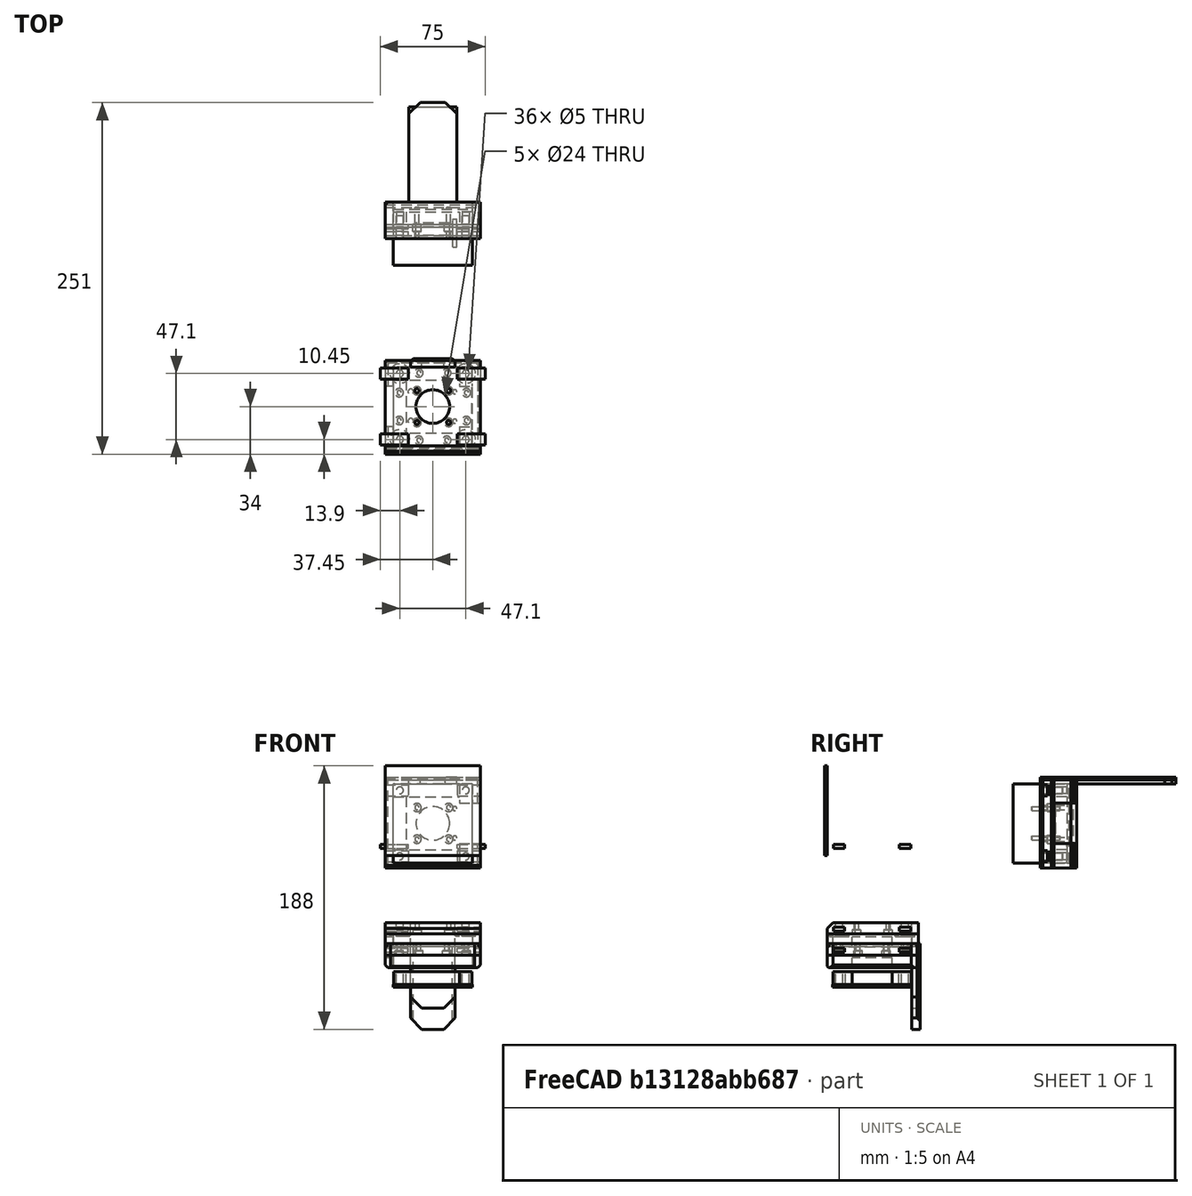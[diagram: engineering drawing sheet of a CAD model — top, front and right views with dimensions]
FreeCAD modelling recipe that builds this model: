
FCSTD DOCUMENT  (FreeCAD 0.19R24276 (Git))
Label: bazovina-part-K-moto-hold_028
License: All rights reserved
LicenseURL: http://en.wikipedia.org/wiki/All_rights_reserved
objects: Part::Cylinder×184, Part::Box×106, Part::Compound×93, Part::Cut×78, Part::Chamfer×16, Part::Common×6, Mesh::Feature×3
note: 483 computed .brp shape members not serialized (recipe doc carries the construction recipe); baked Part::Feature solids carry a one-line shape summary decoded from their .brp

FEATURE [Part::Box] Box131  label="Krychle131"
  AttacherType = Attacher::AttachEngine3D
  Height = 9
  Length = 14.62
  Placement = pos=(-58,38,63) rot=(0,0,1;0rad)
  Width = 10
FEATURE [Part::Cylinder] Cylinder280  label="Válec280"
  Angle = 360
  AttacherType = Attacher::AttachEngine3D
  Height = 50
  Placement = pos=(-23.55,-23.55,20) rot=(0,0,1;0rad)
  Radius = 2.5
FEATURE [Part::Box] Box130  label="Krychle130"
  AttacherType = Attacher::AttachEngine3D
  Height = 9
  Length = 10
  Placement = pos=(-58,-10,63) rot=(0,0,1;0rad)
  Width = 48
FEATURE [Part::Box] Box132  label="Krychle132"
  AttacherType = Attacher::AttachEngine3D
  Height = 9
  Length = 38
  Placement = pos=(-48,-10,63) rot=(0,0,1;0rad)
  Width = 10
FEATURE [Part::Cylinder] Cylinder281  label="Válec281"
  Angle = 360
  AttacherType = Attacher::AttachEngine3D
  Height = 50
  Placement = pos=(23.55,23.55,20) rot=(0,0,1;0rad)
  Radius = 2.5
FEATURE [Part::Box] Box133  label="Krychle133"
  AttacherType = Attacher::AttachEngine3D
  Height = 9
  Length = 14.62
  Placement = pos=(-14.615,38,63) rot=(0,0,1;0rad)
  Width = 10
FEATURE [Part::Cylinder] Cylinder282  label="Válec282"
  Angle = 360
  AttacherType = Attacher::AttachEngine3D
  Height = 50
  Placement = pos=(-23.55,23.55,20) rot=(0,0,1;0rad)
  Radius = 2.5
FEATURE [Part::Box] Box134  label="Krychle134"
  AttacherType = Attacher::AttachEngine3D
  Height = 9
  Length = 10
  Placement = pos=(-10,-10,63) rot=(0,0,1;0rad)
  Width = 48
FEATURE [Part::Compound] Compound277
  Links = -> [Box131,Box134,Box130,Box133,Box132]
  Placement = pos=(29,-19,-4) rot=(0,0,1;0rad)
FEATURE [Part::Cylinder] Cylinder283  label="Válec283"
  Angle = 360
  AttacherType = Attacher::AttachEngine3D
  Height = 50
  Placement = pos=(23.55,-23.55,20) rot=(0,0,1;0rad)
  Radius = 2.5
FEATURE [Part::Compound] Compound276
  Links = -> [Cylinder281,Cylinder283,Cylinder280,Cylinder282]
FEATURE [Part::Cut] Cut125
  Base = -> Compound277
  Placement = pos=(0,198,49) rot=(0.57735,0.57735,-0.57735;2.0944rad)
  Tool = -> Compound276
FEATURE [Part::Box] Box142  label="Krychle142"
  AttacherType = Attacher::AttachEngine3D
  Height = 18
  Length = 64
  Placement = pos=(-32,-34,32) rot=(0,0,1;0rad)
  Width = 68
FEATURE [Part::Cylinder] Cylinder588  label="Válec588"
  Angle = 360
  AttacherType = Attacher::AttachEngine3D
  Height = 20
  Placement = pos=(-7,-34,37) rot=(1,0,0;1.5708rad)
  Radius = 1.5
FEATURE [Part::Cylinder] Cylinder303  label="Válec303"
  Angle = 360
  AttacherType = Attacher::AttachEngine3D
  Height = 20
  Placement = pos=(7,-34,37) rot=(1,0,0;1.5708rad)
  Radius = 1.5
FEATURE [Part::Box] Box143  label="Krychle143"
  AttacherType = Attacher::AttachEngine3D
  Height = 6
  Length = 10
  Placement = pos=(3,-48,70) rot=(0,0,1;0rad)
  Width = 2
FEATURE [Part::Cylinder] Cylinder593  label="Válec593"
  Angle = 360
  AttacherType = Attacher::AttachEngine3D
  Height = 5
  Placement = pos=(2e-15,16,2) rot=(0,0,-1;1.1781rad)
  Radius = 3
FEATURE [Part::Box] Box225  label="Krychle225"
  AttacherType = Attacher::AttachEngine3D
  Height = 8
  Length = 68
  Placement = pos=(-34,-32,24) rot=(0,0,1;0rad)
  Width = 64
FEATURE [Part::Cylinder] Cylinder317  label="Válec317"
  Angle = 360
  AttacherType = Attacher::AttachEngine3D
  Height = 30
  Placement = pos=(-1.2e-14,-16,2) rot=(0,0,1;1.96349rad)
  Radius = 1.5
FEATURE [Part::Box] Box140  label="Krychle140"
  AttacherType = Attacher::AttachEngine3D
  Height = 6
  Length = 10
  Placement = pos=(-11,-48,70) rot=(0,0,1;0rad)
  Width = 2
FEATURE [Part::Box] Box139  label="Krychle139"
  AttacherType = Attacher::AttachEngine3D
  Height = 6
  Length = 10
  Placement = pos=(3,-48,34) rot=(0,0,1;0rad)
  Width = 2
FEATURE [Part::Box] Box223  label="Krychle223"
  AttacherType = Attacher::AttachEngine3D
  Height = 40
  Length = 56.5
  Placement = pos=(-28.25,-28.25,32) rot=(0,0,1;0rad)
  Width = 56.5
FEATURE [Part::Cut] Cut231
  Base = -> Box142
  Tool = -> Box223
FEATURE [Part::Compound] Compound283  label="hrubo_holder010"
  Links = -> [Cut231]
FEATURE [Part::Compound] Compound366  label="hrubo_holder011"
  Links = -> [Compound283]
FEATURE [Part::Box] Box141  label="Krychle141"
  AttacherType = Attacher::AttachEngine3D
  Height = 20
  Length = 28.8
  Placement = pos=(-14.4,-8,34) rot=(0,0,1;0rad)
  Width = 43.38
FEATURE [Part::Cut] Cut230
  Base = -> Compound366
  Placement = pos=(-29,18,30) rot=(0,0,1;0rad)
  Tool = -> Box141
FEATURE [Part::Compound] Compound361
  Links = -> [Cut230]
  Placement = pos=(-18,-29,-30) rot=(0,0,-1;1.5708rad)
FEATURE [Part::Compound] Compound287  label="hrubo_holder_nuovo003"
  Links = -> [Compound361]
FEATURE [Part::Compound] Compound365  label="hrubo_holder012"
  Links = -> [Compound287]
FEATURE [Part::Cylinder] Cylinder305  label="Válec305"
  Angle = 360
  AttacherType = Attacher::AttachEngine3D
  Height = 20
  Placement = pos=(-7,-34,73) rot=(1,0,0;1.5708rad)
  Radius = 1.5
FEATURE [Part::Cylinder] Cylinder306  label="Válec306"
  Angle = 360
  AttacherType = Attacher::AttachEngine3D
  Height = 20
  Placement = pos=(7,-34,73) rot=(1,0,0;1.5708rad)
  Radius = 1.5
FEATURE [Part::Compound] Compound279
  Links = -> [Cylinder303,Cylinder588,Cylinder306,Cylinder305]
FEATURE [Part::Cut] Cut228
  Base = -> Compound365
  Tool = -> Compound279
FEATURE [Part::Cylinder] Cylinder592  label="Válec592"
  Angle = 360
  AttacherType = Attacher::AttachEngine3D
  Height = 4
  Placement = pos=(-23.55,-23.55,26) rot=(0,0,1;0rad)
  Radius = 5
FEATURE [Part::Cylinder] Cylinder600  label="Válec600"
  Angle = 360
  AttacherType = Attacher::AttachEngine3D
  Height = 5
  Placement = pos=(16,0,2) rot=(0,0,1;3.53429rad)
  Radius = 3
FEATURE [Part::Cylinder] Cylinder595  label="Válec595"
  Angle = 360
  AttacherType = Attacher::AttachEngine3D
  Height = 5
  Placement = pos=(-16,7e-15,2) rot=(0,0,1;0.392699rad)
  Radius = 3
FEATURE [Part::Cylinder] Cylinder603  label="Válec603"
  Angle = 360
  AttacherType = Attacher::AttachEngine3D
  Height = 30
  Placement = pos=(2e-15,16,2) rot=(0,0,-1;1.1781rad)
  Radius = 1.5
FEATURE [Part::Cylinder] Cylinder605  label="Válec605"
  Angle = 360
  AttacherType = Attacher::AttachEngine3D
  Height = 4
  Placement = pos=(-23.55,23.55,26) rot=(0,0,1;0rad)
  Radius = 5
FEATURE [Part::Cylinder] Cylinder597  label="Válec597"
  Angle = 360
  AttacherType = Attacher::AttachEngine3D
  Height = 4
  Placement = pos=(23.55,-23.55,26) rot=(0,0,1;0rad)
  Radius = 5
FEATURE [Part::Cylinder] Cylinder601  label="Válec601"
  Angle = 360
  AttacherType = Attacher::AttachEngine3D
  Height = 20
  Placement = pos=(-23.55,23.55,20) rot=(0,0,1;0rad)
  Radius = 2.5
FEATURE [Part::Cylinder] Cylinder594  label="Válec594"
  Angle = 360
  AttacherType = Attacher::AttachEngine3D
  Height = 4
  Placement = pos=(23.55,23.55,26) rot=(0,0,1;0rad)
  Radius = 5
FEATURE [Part::Compound] Compound370
  Links = -> [Cylinder592,Cylinder594,Cylinder597,Cylinder605]
  Placement = pos=(0,0,-50) rot=(0,0,1;0rad)
FEATURE [Part::Box] Box144  label="Krychle144"
  AttacherType = Attacher::AttachEngine3D
  Height = 6
  Length = 10
  Placement = pos=(-11,-48,34) rot=(0,0,1;0rad)
  Width = 2
FEATURE [Part::Compound] Compound362
  Links = -> [Box139,Box144,Box143,Box140]
  Placement = pos=(0,9.75,0) rot=(0,0,1;0rad)
FEATURE [Part::Cut] Cut229  label="motor_holder001"
  Base = -> Cut228
  Tool = -> Compound362
FEATURE [Part::Box] Box227  label="Krychle227"
  AttacherType = Attacher::AttachEngine3D
  Height = 3
  Length = 20
  Placement = pos=(-37.45,19.55,26) rot=(0,0,1;0rad)
  Width = 8
FEATURE [Part::Box] Box228  label="Krychle228"
  AttacherType = Attacher::AttachEngine3D
  Height = 3
  Length = 20
  Placement = pos=(17.55,19.55,26) rot=(0,0,1;0rad)
  Width = 8
FEATURE [Part::Cylinder] Cylinder598  label="Válec598"
  Angle = 360
  AttacherType = Attacher::AttachEngine3D
  Height = 20
  Placement = pos=(-23.55,-23.55,20) rot=(0,0,1;0rad)
  Radius = 2.5
FEATURE [Part::Cylinder] Cylinder599  label="Válec599"
  Angle = 360
  AttacherType = Attacher::AttachEngine3D
  Height = 20
  Placement = pos=(0,0,15) rot=(0,0,1;0rad)
  Radius = 12
FEATURE [Part::Box] Box226  label="Krychle226"
  AttacherType = Attacher::AttachEngine3D
  Height = 3
  Length = 20
  Placement = pos=(17.55,-27.55,26) rot=(0,0,1;0rad)
  Width = 8
FEATURE [Part::Cylinder] Cylinder596  label="Válec596"
  Angle = 360
  AttacherType = Attacher::AttachEngine3D
  Height = 30
  Placement = pos=(-16,7e-15,2) rot=(0,0,1;0.392699rad)
  Radius = 1.5
FEATURE [Part::Box] Box229  label="Krychle229"
  AttacherType = Attacher::AttachEngine3D
  Height = 3
  Length = 20
  Placement = pos=(-37.45,-27.55,26) rot=(0,0,1;0rad)
  Width = 8
FEATURE [Part::Compound] Compound371
  Links = -> [Box228,Box226,Box227,Box229]
FEATURE [Part::Cylinder] Cylinder602  label="Válec602"
  Angle = 360
  AttacherType = Attacher::AttachEngine3D
  Height = 30
  Placement = pos=(16,0,2) rot=(0,0,1;3.53429rad)
  Radius = 1.5
FEATURE [Part::Compound] Compound294
  Links = -> [Cylinder317,Cylinder596,Cylinder603,Cylinder602]
  Placement = pos=(0,0,14) rot=(0,0,1;0.785398rad)
FEATURE [Part::Cut] Cut227
  Base = -> Box225
  Tool = -> Compound294
FEATURE [Part::Cylinder] Cylinder318  label="Válec318"
  Angle = 360
  AttacherType = Attacher::AttachEngine3D
  Height = 5
  Placement = pos=(-1.2e-14,-16,2) rot=(0,0,1;1.96349rad)
  Radius = 3
FEATURE [Part::Compound] Compound368
  Links = -> [Cylinder318,Cylinder595,Cylinder593,Cylinder600]
  Placement = pos=(0,0,27) rot=(0,0,1;0.785398rad)
FEATURE [Part::Cylinder] Cylinder604  label="Válec604"
  Angle = 360
  AttacherType = Attacher::AttachEngine3D
  Height = 20
  Placement = pos=(23.55,23.55,20) rot=(0,0,1;0rad)
  Radius = 2.5
FEATURE [Part::Cylinder] Cylinder606  label="Válec606"
  Angle = 360
  AttacherType = Attacher::AttachEngine3D
  Height = 20
  Placement = pos=(23.55,-23.55,20) rot=(0,0,1;0rad)
  Radius = 2.5
FEATURE [Part::Compound] Compound369
  Links = -> [Cylinder604,Cylinder601,Cylinder598,Cylinder606]
FEATURE [Part::Cut] Cut237
  Base = -> Cut227
  Tool = -> Compound368
FEATURE [Part::Cut] Cut236
  Base = -> Cut237
  Tool = -> Compound369
FEATURE [Part::Cut] Cut235
  Base = -> Cut236
  Tool = -> Compound370
FEATURE [Part::Cut] Cut233
  Base = -> Cut235
  Tool = -> Cylinder599
FEATURE [Part::Cut] Cut234
  Base = -> Cut233
  Tool = -> Compound371
FEATURE [Part::Compound] Compound367  label="novo_moto_holder_hrubo"
  Links = -> [Cut229,Cut234]
  Placement = pos=(0,96,49) rot=(-1,0,0;1.5708rad)
FEATURE [Part::Box] Box244  label="Krychle244"
  AttacherType = Attacher::AttachEngine3D
  Height = 2
  Length = 68
  Placement = pos=(-34,107,80) rot=(0,0,1;0rad)
  Width = 54
FEATURE [Part::Cylinder] Cylinder644  label="Válec644"
  Angle = 360
  AttacherType = Attacher::AttachEngine3D
  Height = 20
  Placement = pos=(15.75,114,38.52) rot=(0,0.707107,0.707107;3.14159rad)
  Radius = 1.5
FEATURE [Part::Box] Box245  label="Krychle245"
  AttacherType = Attacher::AttachEngine3D
  Height = 2.75
  Length = 34
  Placement = pos=(-17,146,77.25) rot=(0,0,1;0rad)
  Width = 68
FEATURE [Part::Cylinder] Cylinder645  label="Válec645"
  Angle = 360
  AttacherType = Attacher::AttachEngine3D
  Height = 20
  Placement = pos=(15.75,114,59.48) rot=(0,0.707107,0.707107;3.14159rad)
  Radius = 1.5
FEATURE [Part::Compound] Compound389
  Links = -> [Cylinder644,Cylinder645]
FEATURE [Part::Cut] Cut253
  Base = -> Compound367
  Tool = -> Compound389
FEATURE [Part::Cut] Cut254
  Base = -> Cut253
  Tool = -> Box244
FEATURE [Part::Compound] Compound391
  Links = -> [Cut254,Box245]
FEATURE [Part::Box] Box246  label="Krychle246"
  AttacherType = Attacher::AttachEngine3D
  Height = 2
  Length = 68
  Placement = pos=(-34,-32,26) rot=(1,0,0;1.5708rad)
  Width = 64
FEATURE [Part::Box] Box247  label="Krychle247"
  AttacherType = Attacher::AttachEngine3D
  Height = 40
  Length = 56.5
  Placement = pos=(-28.25,140.75,20.75) rot=(1,0,0;1.5708rad)
  Width = 56.5
FEATURE [Part::Box] Box248  label="Krychle248"
  AttacherType = Attacher::AttachEngine3D
  Height = 40
  Length = 56.5
  Placement = pos=(-28.25,140.75,20.75) rot=(1,0,0;1.5708rad)
  Width = 56.5
FEATURE [Part::Common] Common
  Base = -> Cut125
  Tool = -> Box247
FEATURE [Part::Box] Box249  label="Krychle249"
  AttacherType = Attacher::AttachEngine3D
  Height = 2
  Length = 56.5
  Placement = pos=(-28.25,130,20.75) rot=(1,0,0;1.5708rad)
  Width = 56.5
FEATURE [Part::Box] Box250  label="Krychle250"
  AttacherType = Attacher::AttachEngine3D
  Height = 20
  Length = 28.8
  Placement = pos=(-14.4,-8,34) rot=(0,0,1;0rad)
  Width = 43.38
FEATURE [Part::Cylinder] Cylinder646  label="Válec646"
  Angle = 360
  AttacherType = Attacher::AttachEngine3D
  Height = 20
  Placement = pos=(-7,-34,73) rot=(1,0,0;1.5708rad)
  Radius = 1.5
FEATURE [Part::Box] Box251  label="Krychle251"
  AttacherType = Attacher::AttachEngine3D
  Height = 40
  Length = 56.5
  Placement = pos=(-28.25,-28.25,34) rot=(0,0,1;0rad)
  Width = 56.5
FEATURE [Part::Cylinder] Cylinder647  label="Válec647"
  Angle = 360
  AttacherType = Attacher::AttachEngine3D
  Height = 30
  Placement = pos=(-1.2e-14,-16,2) rot=(0,0,1;1.96349rad)
  Radius = 1.5
FEATURE [Part::Box] Box252  label="Krychle252"
  AttacherType = Attacher::AttachEngine3D
  Height = 6
  Length = 10
  Placement = pos=(-11,-48,70) rot=(0,0,1;0rad)
  Width = 2
FEATURE [Part::Box] Box253  label="Krychle253"
  AttacherType = Attacher::AttachEngine3D
  Height = 20
  Length = 68
  Placement = pos=(-34,-32,26) rot=(0,0,1;0rad)
  Width = 64
FEATURE [Part::Box] Box254  label="Krychle254"
  AttacherType = Attacher::AttachEngine3D
  Height = 6
  Length = 10
  Placement = pos=(3,-48,34) rot=(0,0,1;0rad)
  Width = 2
FEATURE [Part::Cylinder] Cylinder648  label="Válec648"
  Angle = 360
  AttacherType = Attacher::AttachEngine3D
  Height = 20
  Placement = pos=(7,-34,73) rot=(1,0,0;1.5708rad)
  Radius = 1.5
FEATURE [Part::Box] Box255  label="Krychle255"
  AttacherType = Attacher::AttachEngine3D
  Height = 16
  Length = 64
  Placement = pos=(-32,-34,34) rot=(0,0,1;0rad)
  Width = 68
FEATURE [Part::Cut] Cut257
  Base = -> Box255
  Tool = -> Box251
FEATURE [Part::Compound] Compound393  label="hrubo_holder013"
  Links = -> [Cut257]
FEATURE [Part::Compound] Compound396  label="hrubo_holder014"
  Links = -> [Compound393]
FEATURE [Part::Cut] Cut260
  Base = -> Compound396
  Placement = pos=(-29,18,30) rot=(0,0,1;0rad)
  Tool = -> Box250
FEATURE [Part::Compound] Compound399
  Links = -> [Cut260]
  Placement = pos=(-18,-29,-30) rot=(0,0,-1;1.5708rad)
FEATURE [Part::Compound] Compound392  label="hrubo_holder_nuovo004"
  Links = -> [Compound399]
FEATURE [Part::Compound] Compound404  label="hrubo_holder015"
  Links = -> [Compound392]
FEATURE [Part::Cylinder] Cylinder649  label="Válec649"
  Angle = 360
  AttacherType = Attacher::AttachEngine3D
  Height = 20
  Placement = pos=(-7,-34,37) rot=(1,0,0;1.5708rad)
  Radius = 1.5
FEATURE [Part::Cylinder] Cylinder650  label="Válec650"
  Angle = 360
  AttacherType = Attacher::AttachEngine3D
  Height = 20
  Placement = pos=(7,-34,37) rot=(1,0,0;1.5708rad)
  Radius = 1.5
FEATURE [Part::Compound] Compound400
  Links = -> [Cylinder650,Cylinder649,Cylinder648,Cylinder646]
FEATURE [Part::Cut] Cut256
  Base = -> Compound404
  Tool = -> Compound400
FEATURE [Part::Box] Box256  label="Krychle256"
  AttacherType = Attacher::AttachEngine3D
  Height = 6
  Length = 10
  Placement = pos=(3,-48,70) rot=(0,0,1;0rad)
  Width = 2
FEATURE [Part::Cylinder] Cylinder651  label="Válec651"
  Angle = 360
  AttacherType = Attacher::AttachEngine3D
  Height = 5
  Placement = pos=(2e-15,16,2) rot=(0,0,-1;1.1781rad)
  Radius = 3
FEATURE [Part::Cylinder] Cylinder652  label="Válec652"
  Angle = 360
  AttacherType = Attacher::AttachEngine3D
  Height = 4
  Placement = pos=(23.55,-23.55,26) rot=(0,0,1;0rad)
  Radius = 5
FEATURE [Part::Box] Box257  label="Krychle257"
  AttacherType = Attacher::AttachEngine3D
  Height = 3
  Length = 20
  Placement = pos=(-37.45,19.55,31) rot=(0,0,1;0rad)
  Width = 8
FEATURE [Part::Box] Box258  label="Krychle258"
  AttacherType = Attacher::AttachEngine3D
  Height = 3
  Length = 20
  Placement = pos=(17.55,-27.55,31) rot=(0,0,1;0rad)
  Width = 8
FEATURE [Part::Box] Box259  label="Krychle259"
  AttacherType = Attacher::AttachEngine3D
  Height = 3
  Length = 20
  Placement = pos=(17.55,19.55,31) rot=(0,0,1;0rad)
  Width = 8
FEATURE [Part::Cylinder] Cylinder653  label="Válec653"
  Angle = 360
  AttacherType = Attacher::AttachEngine3D
  Height = 30
  Placement = pos=(-16,7e-15,2) rot=(0,0,1;0.392699rad)
  Radius = 1.5
FEATURE [Part::Cylinder] Cylinder654  label="Válec654"
  Angle = 360
  AttacherType = Attacher::AttachEngine3D
  Height = 20
  Placement = pos=(-23.55,-23.55,20) rot=(0,0,1;0rad)
  Radius = 2.5
FEATURE [Part::Cylinder] Cylinder655  label="Válec655"
  Angle = 360
  AttacherType = Attacher::AttachEngine3D
  Height = 5
  Placement = pos=(-16,7e-15,2) rot=(0,0,1;0.392699rad)
  Radius = 3
FEATURE [Part::Box] Box260  label="Krychle260"
  AttacherType = Attacher::AttachEngine3D
  Height = 3
  Length = 20
  Placement = pos=(-37.45,-27.55,31) rot=(0,0,1;0rad)
  Width = 8
FEATURE [Part::Compound] Compound405
  Links = -> [Box259,Box258,Box257,Box260]
FEATURE [Part::Cylinder] Cylinder656  label="Válec656"
  Angle = 360
  AttacherType = Attacher::AttachEngine3D
  Height = 5
  Placement = pos=(16,0,2) rot=(0,0,1;3.53429rad)
  Radius = 3
FEATURE [Part::Cylinder] Cylinder657  label="Válec657"
  Angle = 360
  AttacherType = Attacher::AttachEngine3D
  Height = 30
  Placement = pos=(2e-15,16,2) rot=(0,0,-1;1.1781rad)
  Radius = 1.5
FEATURE [Part::Cylinder] Cylinder658  label="Válec658"
  Angle = 360
  AttacherType = Attacher::AttachEngine3D
  Height = 4
  Placement = pos=(-23.55,23.55,26) rot=(0,0,1;0rad)
  Radius = 5
FEATURE [Part::Cylinder] Cylinder659  label="Válec659"
  Angle = 360
  AttacherType = Attacher::AttachEngine3D
  Height = 20
  Placement = pos=(-23.55,23.55,20) rot=(0,0,1;0rad)
  Radius = 2.5
FEATURE [Part::Box] Box261  label="Krychle261"
  AttacherType = Attacher::AttachEngine3D
  Height = 6
  Length = 10
  Placement = pos=(-11,-48,34) rot=(0,0,1;0rad)
  Width = 2
FEATURE [Part::Compound] Compound394
  Links = -> [Box254,Box261,Box256,Box252]
  Placement = pos=(0,9.75,0) rot=(0,0,1;0rad)
FEATURE [Part::Cut] Cut259  label="motor_holder002"
  Base = -> Cut256
  Tool = -> Compound394
FEATURE [Part::Cylinder] Cylinder660  label="Válec660"
  Angle = 360
  AttacherType = Attacher::AttachEngine3D
  Height = 20
  Placement = pos=(0,0,15) rot=(0,0,1;0rad)
  Radius = 12
FEATURE [Part::Cylinder] Cylinder661  label="Válec661"
  Angle = 360
  AttacherType = Attacher::AttachEngine3D
  Height = 4
  Placement = pos=(-23.55,-23.55,26) rot=(0,0,1;0rad)
  Radius = 5
FEATURE [Part::Cylinder] Cylinder662  label="Válec662"
  Angle = 360
  AttacherType = Attacher::AttachEngine3D
  Height = 4
  Placement = pos=(23.55,23.55,26) rot=(0,0,1;0rad)
  Radius = 5
FEATURE [Part::Compound] Compound395
  Links = -> [Cylinder661,Cylinder662,Cylinder652,Cylinder658]
  Placement = pos=(0,0,-50) rot=(0,0,1;0rad)
FEATURE [Part::Cylinder] Cylinder663  label="Válec663"
  Angle = 360
  AttacherType = Attacher::AttachEngine3D
  Height = 20
  Placement = pos=(23.55,-23.55,20) rot=(0,0,1;0rad)
  Radius = 2.5
FEATURE [Part::Cylinder] Cylinder664  label="Válec664"
  Angle = 360
  AttacherType = Attacher::AttachEngine3D
  Height = 5
  Placement = pos=(-1.2e-14,-16,2) rot=(0,0,1;1.96349rad)
  Radius = 3
FEATURE [Part::Compound] Compound403
  Links = -> [Cylinder664,Cylinder655,Cylinder651,Cylinder656]
  Placement = pos=(0,0,27) rot=(0,0,1;0.785398rad)
FEATURE [Part::Cylinder] Cylinder665  label="Válec665"
  Angle = 360
  AttacherType = Attacher::AttachEngine3D
  Height = 20
  Placement = pos=(15.75,114,59.48) rot=(0,0.707107,0.707107;3.14159rad)
  Radius = 1.5
FEATURE [Part::Box] Box262  label="Krychle262"
  AttacherType = Attacher::AttachEngine3D
  Height = 2
  Length = 68
  Placement = pos=(-34,107,80) rot=(0,0,1;0rad)
  Width = 54
FEATURE [Part::Cylinder] Cylinder666  label="Válec666"
  Angle = 360
  AttacherType = Attacher::AttachEngine3D
  Height = 20
  Placement = pos=(15.75,114,38.52) rot=(0,0.707107,0.707107;3.14159rad)
  Radius = 1.5
FEATURE [Part::Compound] Compound397
  Links = -> [Cylinder666,Cylinder665]
FEATURE [Part::Cylinder] Cylinder667  label="Válec667"
  Angle = 360
  AttacherType = Attacher::AttachEngine3D
  Height = 20
  Placement = pos=(23.55,23.55,20) rot=(0,0,1;0rad)
  Radius = 2.5
FEATURE [Part::Compound] Compound402
  Links = -> [Cylinder667,Cylinder659,Cylinder654,Cylinder663]
FEATURE [Part::Cylinder] Cylinder668  label="Válec668"
  Angle = 360
  AttacherType = Attacher::AttachEngine3D
  Height = 30
  Placement = pos=(16,0,2) rot=(0,0,1;3.53429rad)
  Radius = 1.5
FEATURE [Part::Compound] Compound398
  Links = -> [Cylinder647,Cylinder653,Cylinder657,Cylinder668]
  Placement = pos=(0,0,14) rot=(0,0,1;0.785398rad)
FEATURE [Part::Cut] Cut255
  Base = -> Box253
  Tool = -> Compound398
FEATURE [Part::Cut] Cut265
  Base = -> Cut255
  Tool = -> Compound403
FEATURE [Part::Cut] Cut266
  Base = -> Cut265
  Tool = -> Compound402
FEATURE [Part::Cut] Cut262
  Base = -> Cut266
  Tool = -> Compound395
FEATURE [Part::Cut] Cut261
  Base = -> Cut262
  Tool = -> Cylinder660
FEATURE [Part::Cut] Cut258
  Base = -> Cut261
  Tool = -> Compound405
FEATURE [Part::Compound] Compound401  label="novo_moto_holder_hrubo001"
  Links = -> [Cut259,Cut258]
  Placement = pos=(0,96,49) rot=(-1,0,0;1.5708rad)
FEATURE [Part::Cut] Cut264
  Base = -> Compound401
  Tool = -> Compound397
FEATURE [Part::Cut] Cut263
  Base = -> Cut264
  Tool = -> Box262
FEATURE [Part::Cylinder] Cylinder669  label="Válec669"
  Angle = 360
  AttacherType = Attacher::AttachEngine3D
  Height = 5
  Placement = pos=(2e-15,16,2) rot=(0,0,-1;1.1781rad)
  Radius = 3
FEATURE [Part::Box] Box263  label="Krychle263"
  AttacherType = Attacher::AttachEngine3D
  Height = 8
  Length = 68
  Placement = pos=(-34,-32,26) rot=(0,0,1;0rad)
  Width = 64
FEATURE [Part::Box] Box264  label="Krychle264"
  AttacherType = Attacher::AttachEngine3D
  Height = 3
  Length = 20
  Placement = pos=(17.55,19.55,31) rot=(0,0,1;0rad)
  Width = 8
FEATURE [Part::Box] Box265  label="Krychle265"
  AttacherType = Attacher::AttachEngine3D
  Height = 3
  Length = 20
  Placement = pos=(-37.45,19.55,31) rot=(0,0,1;0rad)
  Width = 8
FEATURE [Part::Box] Box266  label="Krychle266"
  AttacherType = Attacher::AttachEngine3D
  Height = 3
  Length = 20
  Placement = pos=(17.55,-27.55,31) rot=(0,0,1;0rad)
  Width = 8
FEATURE [Part::Cylinder] Cylinder670  label="Válec670"
  Angle = 360
  AttacherType = Attacher::AttachEngine3D
  Height = 4
  Placement = pos=(23.55,-23.55,26) rot=(0,0,1;0rad)
  Radius = 5
FEATURE [Part::Cylinder] Cylinder671  label="Válec671"
  Angle = 360
  AttacherType = Attacher::AttachEngine3D
  Height = 30
  Placement = pos=(-1.2e-14,-16,2) rot=(0,0,1;1.96349rad)
  Radius = 1.5
FEATURE [Part::Cylinder] Cylinder672  label="Válec672"
  Angle = 360
  AttacherType = Attacher::AttachEngine3D
  Height = 4
  Placement = pos=(23.55,23.55,26) rot=(0,0,1;0rad)
  Radius = 5
FEATURE [Part::Cylinder] Cylinder673  label="Válec673"
  Angle = 360
  AttacherType = Attacher::AttachEngine3D
  Height = 20
  Placement = pos=(-23.55,-23.55,20) rot=(0,0,1;0rad)
  Radius = 2.5
FEATURE [Part::Cylinder] Cylinder674  label="Válec674"
  Angle = 360
  AttacherType = Attacher::AttachEngine3D
  Height = 4
  Placement = pos=(-23.55,23.55,26) rot=(0,0,1;0rad)
  Radius = 5
FEATURE [Part::Cylinder] Cylinder675  label="Válec675"
  Angle = 360
  AttacherType = Attacher::AttachEngine3D
  Height = 4
  Placement = pos=(-23.55,-23.55,26) rot=(0,0,1;0rad)
  Radius = 5
FEATURE [Part::Compound] Compound406
  Links = -> [Cylinder675,Cylinder672,Cylinder670,Cylinder674]
  Placement = pos=(0,0,-50) rot=(0,0,1;0rad)
FEATURE [Part::Cylinder] Cylinder676  label="Válec676"
  Angle = 360
  AttacherType = Attacher::AttachEngine3D
  Height = 20
  Placement = pos=(23.55,-23.55,20) rot=(0,0,1;0rad)
  Radius = 2.5
FEATURE [Part::Cylinder] Cylinder677  label="Válec677"
  Angle = 360
  AttacherType = Attacher::AttachEngine3D
  Height = 5
  Placement = pos=(-1.2e-14,-16,2) rot=(0,0,1;1.96349rad)
  Radius = 3
FEATURE [Part::Cylinder] Cylinder678  label="Válec678"
  Angle = 360
  AttacherType = Attacher::AttachEngine3D
  Height = 30
  Placement = pos=(2e-15,16,2) rot=(0,0,-1;1.1781rad)
  Radius = 1.5
FEATURE [Part::Cylinder] Cylinder679  label="Válec679"
  Angle = 360
  AttacherType = Attacher::AttachEngine3D
  Height = 30
  Placement = pos=(-16,7e-15,2) rot=(0,0,1;0.392699rad)
  Radius = 1.5
FEATURE [Part::Cylinder] Cylinder680  label="Válec680"
  Angle = 360
  AttacherType = Attacher::AttachEngine3D
  Height = 5
  Placement = pos=(16,0,2) rot=(0,0,1;3.53429rad)
  Radius = 3
FEATURE [Part::Cylinder] Cylinder681  label="Válec681"
  Angle = 360
  AttacherType = Attacher::AttachEngine3D
  Height = 5
  Placement = pos=(-16,7e-15,2) rot=(0,0,1;0.392699rad)
  Radius = 3
FEATURE [Part::Compound] Compound408
  Links = -> [Cylinder677,Cylinder681,Cylinder669,Cylinder680]
  Placement = pos=(0,0,27) rot=(0,0,1;0.785398rad)
FEATURE [Part::Cylinder] Cylinder682  label="Válec682"
  Angle = 360
  AttacherType = Attacher::AttachEngine3D
  Height = 20
  Placement = pos=(0,0,15) rot=(0,0,1;0rad)
  Radius = 12
FEATURE [Part::Cylinder] Cylinder683  label="Válec683"
  Angle = 360
  AttacherType = Attacher::AttachEngine3D
  Height = 20
  Placement = pos=(-23.55,23.55,20) rot=(0,0,1;0rad)
  Radius = 2.5
FEATURE [Part::Box] Box267  label="Krychle267"
  AttacherType = Attacher::AttachEngine3D
  Height = 3
  Length = 20
  Placement = pos=(-37.45,-27.55,31) rot=(0,0,1;0rad)
  Width = 8
FEATURE [Part::Compound] Compound410
  Links = -> [Box264,Box266,Box265,Box267]
  Placement = pos=(0,0,-4) rot=(0,0,1;0rad)
FEATURE [Part::Cylinder] Cylinder684  label="Válec684"
  Angle = 360
  AttacherType = Attacher::AttachEngine3D
  Height = 20
  Placement = pos=(23.55,23.55,20) rot=(0,0,1;0rad)
  Radius = 2.5
FEATURE [Part::Compound] Compound407
  Links = -> [Cylinder684,Cylinder683,Cylinder673,Cylinder676]
FEATURE [Part::Cylinder] Cylinder685  label="Válec685"
  Angle = 360
  AttacherType = Attacher::AttachEngine3D
  Height = 30
  Placement = pos=(16,0,2) rot=(0,0,1;3.53429rad)
  Radius = 1.5
FEATURE [Part::Compound] Compound409
  Links = -> [Cylinder671,Cylinder679,Cylinder678,Cylinder685]
  Placement = pos=(0,0,14) rot=(0,0,1;0.785398rad)
FEATURE [Part::Cut] Cut271
  Base = -> Box263
  Tool = -> Compound409
FEATURE [Part::Cut] Cut270
  Base = -> Cut271
  Tool = -> Compound408
FEATURE [Part::Cut] Cut272
  Base = -> Cut270
  Tool = -> Compound407
FEATURE [Part::Cut] Cut269
  Base = -> Cut272
  Tool = -> Compound406
FEATURE [Part::Cut] Cut268
  Base = -> Cut269
  Tool = -> Cylinder682
FEATURE [Part::Cut] Cut267
  Base = -> Cut268
  Placement = pos=(0,0,-100) rot=(0,0,1;0rad)
  Tool = -> Compound410
FEATURE [Part::Cylinder] Cylinder686  label="Válec686"
  Angle = 360
  AttacherType = Attacher::AttachEngine3D
  Height = 20
  Placement = pos=(15.75,114,38.52) rot=(0,0.707107,0.707107;3.14159rad)
  Radius = 1.5
FEATURE [Part::Cylinder] Cylinder687  label="Válec687"
  Angle = 360
  AttacherType = Attacher::AttachEngine3D
  Height = 20
  Placement = pos=(15.75,114,59.48) rot=(0,0.707107,0.707107;3.14159rad)
  Radius = 1.5
FEATURE [Part::Compound] Compound411
  Links = -> [Cylinder686,Cylinder687]
  Placement = pos=(0,49,-200) rot=(1,0,0;1.5708rad)
FEATURE [Part::Cut] Cut
  Base = -> Cut267
  Tool = -> Compound411
FEATURE [Part::Box] Box268  label="Krychle268"
  AttacherType = Attacher::AttachEngine3D
  Height = 2
  Length = 56.5
  Placement = pos=(-28.25,-28.25,-68) rot=(0,0,1;0rad)
  Width = 56.5
FEATURE [Part::Common] Common001
  Base = -> Cut
  Tool = -> Box268
FEATURE [Part::Box] Box275  label="Krychle275"
  AttacherType = Attacher::AttachEngine3D
  Height = 9
  Length = 14.62
  Placement = pos=(-58,38,63) rot=(0,0,1;0rad)
  Width = 10
FEATURE [Part::Cylinder] Cylinder707  label="Válec707"
  Angle = 360
  AttacherType = Attacher::AttachEngine3D
  Height = 50
  Placement = pos=(-23.55,-23.55,20) rot=(0,0,1;0rad)
  Radius = 2.5
FEATURE [Part::Box] Box276  label="Krychle276"
  AttacherType = Attacher::AttachEngine3D
  Height = 9
  Length = 10
  Placement = pos=(-58,-10,63) rot=(0,0,1;0rad)
  Width = 48
FEATURE [Part::Box] Box277  label="Krychle277"
  AttacherType = Attacher::AttachEngine3D
  Height = 9
  Length = 38
  Placement = pos=(-48,-10,63) rot=(0,0,1;0rad)
  Width = 10
FEATURE [Part::Box] Box278  label="Krychle278"
  AttacherType = Attacher::AttachEngine3D
  Height = 9
  Length = 10
  Placement = pos=(-10,-10,63) rot=(0,0,1;0rad)
  Width = 48
FEATURE [Part::Cylinder] Cylinder708  label="Válec708"
  Angle = 360
  AttacherType = Attacher::AttachEngine3D
  Height = 50
  Placement = pos=(23.55,-23.55,20) rot=(0,0,1;0rad)
  Radius = 2.5
FEATURE [Part::Cylinder] Cylinder709  label="Válec709"
  Angle = 360
  AttacherType = Attacher::AttachEngine3D
  Height = 50
  Placement = pos=(23.55,23.55,20) rot=(0,0,1;0rad)
  Radius = 2.5
FEATURE [Part::Box] Box279  label="Krychle279"
  AttacherType = Attacher::AttachEngine3D
  Height = 9
  Length = 14.62
  Placement = pos=(-14.615,38,63) rot=(0,0,1;0rad)
  Width = 10
FEATURE [Part::Compound] Compound418
  Links = -> [Box275,Box278,Box276,Box279,Box277]
  Placement = pos=(29,-19,-4) rot=(0,0,1;0rad)
FEATURE [Part::Cylinder] Cylinder710  label="Válec710"
  Angle = 360
  AttacherType = Attacher::AttachEngine3D
  Height = 50
  Placement = pos=(-23.55,23.55,20) rot=(0,0,1;0rad)
  Radius = 2.5
FEATURE [Part::Compound] Compound419
  Links = -> [Cylinder709,Cylinder708,Cylinder707,Cylinder710]
FEATURE [Part::Cut] Cut280
  Base = -> Compound418
  Placement = pos=(0,198,49) rot=(0.57735,0.57735,-0.57735;2.0944rad)
  Tool = -> Compound419
FEATURE [Part::Box] Box280  label="Krychle280"
  AttacherType = Attacher::AttachEngine3D
  Height = 2
  Length = 56
  Placement = pos=(-28,130,21) rot=(1,0,0;1.5708rad)
  Width = 56
FEATURE [Part::Common] Common003
  Base = -> Cut280
  Placement = pos=(0,49,-196) rot=(1,0,0;1.5708rad)
  Tool = -> Box280
FEATURE [Part::Cylinder] Cylinder711  label="Válec711"
  Angle = 360
  AttacherType = Attacher::AttachEngine3D
  Height = 20
  Placement = pos=(15.75,114,59.48) rot=(0,0.707107,0.707107;3.14159rad)
  Radius = 1.5
FEATURE [Part::Cylinder] Cylinder712  label="Válec712"
  Angle = 360
  AttacherType = Attacher::AttachEngine3D
  Height = 20
  Placement = pos=(15.75,114,38.52) rot=(0,0.707107,0.707107;3.14159rad)
  Radius = 1.5
FEATURE [Part::Compound] Compound420
  Links = -> [Cylinder712,Cylinder711]
FEATURE [Part::Box] Box281  label="Krychle281"
  AttacherType = Attacher::AttachEngine3D
  Height = 3
  Length = 20
  Placement = pos=(-37.45,19.55,31) rot=(0,0,1;0rad)
  Width = 8
FEATURE [Part::Box] Box282  label="Krychle282"
  AttacherType = Attacher::AttachEngine3D
  Height = 3
  Length = 20
  Placement = pos=(17.55,19.55,31) rot=(0,0,1;0rad)
  Width = 8
FEATURE [Part::Box] Box283  label="Krychle283"
  AttacherType = Attacher::AttachEngine3D
  Height = 3
  Length = 20
  Placement = pos=(17.55,-27.55,31) rot=(0,0,1;0rad)
  Width = 8
FEATURE [Part::Box] Box284  label="Krychle284"
  AttacherType = Attacher::AttachEngine3D
  Height = 3
  Length = 20
  Placement = pos=(-37.45,-27.55,31) rot=(0,0,1;0rad)
  Width = 8
FEATURE [Part::Compound] Compound421
  Links = -> [Box282,Box283,Box281,Box284]
FEATURE [Part::Box] Box285  label="Krychle285"
  AttacherType = Attacher::AttachEngine3D
  Height = 2
  Length = 68
  Placement = pos=(-34,107,80) rot=(0,0,1;0rad)
  Width = 54
FEATURE [Part::Cut] Cut281  label="hold-out"
  Base = -> Compound391
  Tool = -> Box285
FEATURE [Part::Cylinder] Cylinder713  label="Válec713"
  Angle = 360
  AttacherType = Attacher::AttachEngine3D
  Height = 20
  Placement = pos=(-7,-34,37) rot=(1,0,0;1.5708rad)
  Radius = 1.5
FEATURE [Part::Cylinder] Cylinder714  label="Válec714"
  Angle = 360
  AttacherType = Attacher::AttachEngine3D
  Height = 5
  Placement = pos=(2e-15,16,2) rot=(0,0,-1;1.1781rad)
  Radius = 3
FEATURE [Part::Box] Box286  label="Krychle286"
  AttacherType = Attacher::AttachEngine3D
  Height = 6
  Length = 10
  Placement = pos=(3,-48,70) rot=(0,0,1;0rad)
  Width = 2
FEATURE [Part::Box] Box287  label="Krychle287"
  AttacherType = Attacher::AttachEngine3D
  Height = 8
  Length = 68
  Placement = pos=(-34,-32,24) rot=(0,0,1;0rad)
  Width = 64
FEATURE [Part::Cylinder] Cylinder715  label="Válec715"
  Angle = 360
  AttacherType = Attacher::AttachEngine3D
  Height = 20
  Placement = pos=(7,-34,37) rot=(1,0,0;1.5708rad)
  Radius = 1.5
FEATURE [Part::Cylinder] Cylinder716  label="Válec716"
  Angle = 360
  AttacherType = Attacher::AttachEngine3D
  Height = 30
  Placement = pos=(-1.2e-14,-16,2) rot=(0,0,1;1.96349rad)
  Radius = 1.5
FEATURE [Part::Box] Box288  label="Krychle288"
  AttacherType = Attacher::AttachEngine3D
  Height = 6
  Length = 10
  Placement = pos=(-11,-48,70) rot=(0,0,1;0rad)
  Width = 2
FEATURE [Part::Box] Box289  label="Krychle289"
  AttacherType = Attacher::AttachEngine3D
  Height = 6
  Length = 10
  Placement = pos=(3,-48,34) rot=(0,0,1;0rad)
  Width = 2
FEATURE [Part::Box] Box290  label="Krychle290"
  AttacherType = Attacher::AttachEngine3D
  Height = 40
  Length = 56.5
  Placement = pos=(-28.25,-28.25,32) rot=(0,0,1;0rad)
  Width = 56.5
FEATURE [Part::Box] Box291  label="Krychle291"
  AttacherType = Attacher::AttachEngine3D
  Height = 18
  Length = 64
  Placement = pos=(-32,-34,32) rot=(0,0,1;0rad)
  Width = 68
FEATURE [Part::Cut] Cut293
  Base = -> Box291
  Tool = -> Box290
FEATURE [Part::Compound] Compound429  label="hrubo_holder018"
  Links = -> [Cut293]
FEATURE [Part::Compound] Compound422  label="hrubo_holder016"
  Links = -> [Compound429]
FEATURE [Part::Box] Box292  label="Krychle292"
  AttacherType = Attacher::AttachEngine3D
  Height = 20
  Length = 28.8
  Placement = pos=(-14.4,-8,34) rot=(0,0,1;0rad)
  Width = 43.38
FEATURE [Part::Cut] Cut283
  Base = -> Compound422
  Placement = pos=(-29,18,30) rot=(0,0,1;0rad)
  Tool = -> Box292
FEATURE [Part::Compound] Compound435
  Links = -> [Cut283]
  Placement = pos=(-18,-29,-30) rot=(0,0,-1;1.5708rad)
FEATURE [Part::Compound] Compound423  label="hrubo_holder_nuovo005"
  Links = -> [Compound435]
FEATURE [Part::Compound] Compound428  label="hrubo_holder017"
  Links = -> [Compound423]
FEATURE [Part::Cylinder] Cylinder717  label="Válec717"
  Angle = 360
  AttacherType = Attacher::AttachEngine3D
  Height = 20
  Placement = pos=(-7,-34,73) rot=(1,0,0;1.5708rad)
  Radius = 1.5
FEATURE [Part::Cylinder] Cylinder718  label="Válec718"
  Angle = 360
  AttacherType = Attacher::AttachEngine3D
  Height = 4
  Placement = pos=(23.55,23.55,26) rot=(0,0,1;0rad)
  Radius = 5
FEATURE [Part::Cylinder] Cylinder719  label="Válec719"
  Angle = 360
  AttacherType = Attacher::AttachEngine3D
  Height = 4
  Placement = pos=(-23.55,23.55,26) rot=(0,0,1;0rad)
  Radius = 5
FEATURE [Part::Box] Box293  label="Krychle293"
  AttacherType = Attacher::AttachEngine3D
  Height = 3
  Length = 20
  Placement = pos=(-37.45,19.55,26) rot=(0,0,1;0rad)
  Width = 8
FEATURE [Part::Box] Box294  label="Krychle294"
  AttacherType = Attacher::AttachEngine3D
  Height = 3
  Length = 20
  Placement = pos=(17.55,19.55,26) rot=(0,0,1;0rad)
  Width = 8
FEATURE [Part::Cylinder] Cylinder720  label="Válec720"
  Angle = 360
  AttacherType = Attacher::AttachEngine3D
  Height = 20
  Placement = pos=(-23.55,-23.55,20) rot=(0,0,1;0rad)
  Radius = 2.5
FEATURE [Part::Cylinder] Cylinder721  label="Válec721"
  Angle = 360
  AttacherType = Attacher::AttachEngine3D
  Height = 5
  Placement = pos=(16,0,2) rot=(0,0,1;3.53429rad)
  Radius = 3
FEATURE [Part::Cylinder] Cylinder722  label="Válec722"
  Angle = 360
  AttacherType = Attacher::AttachEngine3D
  Height = 20
  Placement = pos=(0,0,15) rot=(0,0,1;0rad)
  Radius = 12
FEATURE [Part::Box] Box295  label="Krychle295"
  AttacherType = Attacher::AttachEngine3D
  Height = 6
  Length = 10
  Placement = pos=(-11,-48,34) rot=(0,0,1;0rad)
  Width = 2
FEATURE [Part::Compound] Compound431
  Links = -> [Box289,Box295,Box286,Box288]
  Placement = pos=(0,9.75,0) rot=(0,0,1;0rad)
FEATURE [Part::Cylinder] Cylinder723  label="Válec723"
  Angle = 360
  AttacherType = Attacher::AttachEngine3D
  Height = 5
  Placement = pos=(-16,7e-15,2) rot=(0,0,1;0.392699rad)
  Radius = 3
FEATURE [Part::Cylinder] Cylinder724  label="Válec724"
  Angle = 360
  AttacherType = Attacher::AttachEngine3D
  Height = 4
  Placement = pos=(-23.55,-23.55,26) rot=(0,0,1;0rad)
  Radius = 5
FEATURE [Part::Cylinder] Cylinder725  label="Válec725"
  Angle = 360
  AttacherType = Attacher::AttachEngine3D
  Height = 20
  Placement = pos=(7,-34,73) rot=(1,0,0;1.5708rad)
  Radius = 1.5
FEATURE [Part::Compound] Compound432
  Links = -> [Cylinder715,Cylinder713,Cylinder725,Cylinder717]
FEATURE [Part::Cut] Cut284
  Base = -> Compound428
  Tool = -> Compound432
FEATURE [Part::Cut] Cut285  label="motor_holder003"
  Base = -> Cut284
  Tool = -> Compound431
FEATURE [Part::Cylinder] Cylinder726  label="Válec726"
  Angle = 360
  AttacherType = Attacher::AttachEngine3D
  Height = 4
  Placement = pos=(23.55,-23.55,26) rot=(0,0,1;0rad)
  Radius = 5
FEATURE [Part::Compound] Compound426
  Links = -> [Cylinder724,Cylinder718,Cylinder726,Cylinder719]
  Placement = pos=(0,0,-50) rot=(0,0,1;0rad)
FEATURE [Part::Cylinder] Cylinder727  label="Válec727"
  Angle = 360
  AttacherType = Attacher::AttachEngine3D
  Height = 30
  Placement = pos=(2e-15,16,2) rot=(0,0,-1;1.1781rad)
  Radius = 1.5
FEATURE [Part::Cylinder] Cylinder728  label="Válec728"
  Angle = 360
  AttacherType = Attacher::AttachEngine3D
  Height = 20
  Placement = pos=(-23.55,23.55,20) rot=(0,0,1;0rad)
  Radius = 2.5
FEATURE [Part::Cylinder] Cylinder729  label="Válec729"
  Angle = 360
  AttacherType = Attacher::AttachEngine3D
  Height = 20
  Placement = pos=(23.55,-23.55,20) rot=(0,0,1;0rad)
  Radius = 2.5
FEATURE [Part::Cylinder] Cylinder730  label="Válec730"
  Angle = 360
  AttacherType = Attacher::AttachEngine3D
  Height = 5
  Placement = pos=(-1.2e-14,-16,2) rot=(0,0,1;1.96349rad)
  Radius = 3
FEATURE [Part::Compound] Compound436
  Links = -> [Cylinder730,Cylinder723,Cylinder714,Cylinder721]
  Placement = pos=(0,0,27) rot=(0,0,1;0.785398rad)
FEATURE [Part::Cylinder] Cylinder731  label="Válec731"
  Angle = 360
  AttacherType = Attacher::AttachEngine3D
  Height = 20
  Placement = pos=(23.55,23.55,20) rot=(0,0,1;0rad)
  Radius = 2.5
FEATURE [Part::Compound] Compound434
  Links = -> [Cylinder731,Cylinder728,Cylinder720,Cylinder729]
FEATURE [Part::Box] Box296  label="Krychle296"
  AttacherType = Attacher::AttachEngine3D
  Height = 2.75
  Length = 34
  Placement = pos=(-17,146,77.25) rot=(0,0,1;0rad)
  Width = 71
FEATURE [Part::Cylinder] Cylinder732  label="Válec732"
  Angle = 360
  AttacherType = Attacher::AttachEngine3D
  Height = 20
  Placement = pos=(15.75,114,59.48) rot=(0,0.707107,0.707107;3.14159rad)
  Radius = 1.5
FEATURE [Part::Cylinder] Cylinder733  label="Válec733"
  Angle = 360
  AttacherType = Attacher::AttachEngine3D
  Height = 30
  Placement = pos=(-16,7e-15,2) rot=(0,0,1;0.392699rad)
  Radius = 1.5
FEATURE [Part::Cylinder] Cylinder734  label="Válec734"
  Angle = 360
  AttacherType = Attacher::AttachEngine3D
  Height = 30
  Placement = pos=(16,0,2) rot=(0,0,1;3.53429rad)
  Radius = 1.5
FEATURE [Part::Compound] Compound424
  Links = -> [Cylinder716,Cylinder733,Cylinder727,Cylinder734]
  Placement = pos=(0,0,14) rot=(0,0,1;0.785398rad)
FEATURE [Part::Cut] Cut290
  Base = -> Box287
  Tool = -> Compound424
FEATURE [Part::Cut] Cut287
  Base = -> Cut290
  Tool = -> Compound436
FEATURE [Part::Cut] Cut294
  Base = -> Cut287
  Tool = -> Compound434
FEATURE [Part::Cut] Cut288
  Base = -> Cut294
  Tool = -> Compound426
FEATURE [Part::Cut] Cut289
  Base = -> Cut288
  Tool = -> Cylinder722
FEATURE [Part::Box] Box297  label="Krychle297"
  AttacherType = Attacher::AttachEngine3D
  Height = 3
  Length = 20
  Placement = pos=(17.55,-27.55,26) rot=(0,0,1;0rad)
  Width = 8
FEATURE [Part::Box] Box298  label="Krychle298"
  AttacherType = Attacher::AttachEngine3D
  Height = 3
  Length = 20
  Placement = pos=(-37.45,-27.55,26) rot=(0,0,1;0rad)
  Width = 8
FEATURE [Part::Compound] Compound430
  Links = -> [Box294,Box297,Box293,Box298]
FEATURE [Part::Cut] Cut286
  Base = -> Cut289
  Tool = -> Compound430
FEATURE [Part::Compound] Compound433  label="novo_moto_holder_hrubo002"
  Links = -> [Cut285,Cut286]
  Placement = pos=(0,96,49) rot=(-1,0,0;1.5708rad)
FEATURE [Part::Box] Box299  label="Krychle299"
  AttacherType = Attacher::AttachEngine3D
  Height = 2
  Length = 68
  Placement = pos=(-34,107,80) rot=(0,0,1;0rad)
  Width = 54
FEATURE [Part::Cylinder] Cylinder735  label="Válec735"
  Angle = 360
  AttacherType = Attacher::AttachEngine3D
  Height = 20
  Placement = pos=(15.75,114,38.52) rot=(0,0.707107,0.707107;3.14159rad)
  Radius = 1.5
FEATURE [Part::Compound] Compound425
  Links = -> [Cylinder735,Cylinder732]
FEATURE [Part::Cut] Cut291
  Base = -> Compound433
  Tool = -> Compound425
FEATURE [Part::Cut] Cut292
  Base = -> Cut291
  Tool = -> Box299
FEATURE [Part::Compound] Compound427
  Links = -> [Cut292,Box296]
FEATURE [Part::Box] Box300  label="Krychle300"
  AttacherType = Attacher::AttachEngine3D
  Height = 2
  Length = 68
  Placement = pos=(-34,107,80) rot=(0,0,1;0rad)
  Width = 54
FEATURE [Part::Cut] Cut282
  Base = -> Compound427
  Tool = -> Box300
FEATURE [Part::Chamfer] Chamfer
  Base = -> Cut282
  Edges = 4 edges r=2: [Edge2,Edge7,Edge8,Edge16]
FEATURE [Part::Chamfer] Chamfer001
  Base = -> Chamfer
  Edges = 1 edges r=2: [Edge72]
FEATURE [Part::Chamfer] Chamfer002  label="bazovina-part-K_hold-out"
  Base = -> Chamfer001
  Edges = 2 edges r=8: [Edge169,Edge174]
FEATURE [Part::Box] Box274  label="Krychle274"
  AttacherType = Attacher::AttachEngine3D
  Height = 2
  Length = 56
  Placement = pos=(-28,-28,-68) rot=(0,0,1;0rad)
  Width = 56
FEATURE [Part::Cylinder] Cylinder704  label="Válec704"
  Angle = 360
  AttacherType = Attacher::AttachEngine3D
  Height = 20
  Placement = pos=(15.75,114,59.48) rot=(0,0.707107,0.707107;3.14159rad)
  Radius = 1.5
FEATURE [Part::Cylinder] Cylinder705  label="Válec705"
  Angle = 360
  AttacherType = Attacher::AttachEngine3D
  Height = 20
  Placement = pos=(15.75,114,38.52) rot=(0,0.707107,0.707107;3.14159rad)
  Radius = 1.5
FEATURE [Part::Compound] Compound417
  Links = -> [Cylinder705,Cylinder704]
  Placement = pos=(0,49,-200) rot=(1,0,0;1.5708rad)
FEATURE [Part::Box] Box273  label="Krychle273"
  AttacherType = Attacher::AttachEngine3D
  Height = 3
  Length = 20
  Placement = pos=(-37.45,-27.55,31) rot=(0,0,1;0rad)
  Width = 8
FEATURE [Part::Box] Box271  label="Krychle271"
  AttacherType = Attacher::AttachEngine3D
  Height = 3
  Length = 20
  Placement = pos=(-37.45,19.55,31) rot=(0,0,1;0rad)
  Width = 8
FEATURE [Part::Box] Box272  label="Krychle272"
  AttacherType = Attacher::AttachEngine3D
  Height = 3
  Length = 20
  Placement = pos=(17.55,-27.55,31) rot=(0,0,1;0rad)
  Width = 8
FEATURE [Part::Box] Box269  label="Krychle269"
  AttacherType = Attacher::AttachEngine3D
  Height = 3
  Length = 20
  Placement = pos=(17.55,19.55,31) rot=(0,0,1;0rad)
  Width = 8
FEATURE [Part::Compound] Compound413
  Links = -> [Box269,Box272,Box271,Box273]
  Placement = pos=(0,0,-4) rot=(0,0,1;0rad)
FEATURE [Part::Cylinder] Cylinder697  label="Válec697"
  Angle = 360
  AttacherType = Attacher::AttachEngine3D
  Height = 20
  Placement = pos=(0,0,15) rot=(0,0,1;0rad)
  Radius = 12
FEATURE [Part::Cylinder] Cylinder693  label="Válec693"
  Angle = 360
  AttacherType = Attacher::AttachEngine3D
  Height = 4
  Placement = pos=(-23.55,23.55,26) rot=(0,0,1;0rad)
  Radius = 5
FEATURE [Part::Cylinder] Cylinder689  label="Válec689"
  Angle = 360
  AttacherType = Attacher::AttachEngine3D
  Height = 4
  Placement = pos=(23.55,-23.55,26) rot=(0,0,1;0rad)
  Radius = 5
FEATURE [Part::Cylinder] Cylinder702  label="Válec702"
  Angle = 360
  AttacherType = Attacher::AttachEngine3D
  Height = 4
  Placement = pos=(23.55,23.55,26) rot=(0,0,1;0rad)
  Radius = 5
FEATURE [Part::Cylinder] Cylinder698  label="Válec698"
  Angle = 360
  AttacherType = Attacher::AttachEngine3D
  Height = 4
  Placement = pos=(-23.55,-23.55,26) rot=(0,0,1;0rad)
  Radius = 5
FEATURE [Part::Compound] Compound415
  Links = -> [Cylinder698,Cylinder702,Cylinder689,Cylinder693]
  Placement = pos=(0,0,-50) rot=(0,0,1;0rad)
FEATURE [Part::Cylinder] Cylinder694  label="Válec694"
  Angle = 360
  AttacherType = Attacher::AttachEngine3D
  Height = 20
  Placement = pos=(23.55,-23.55,20) rot=(0,0,1;0rad)
  Radius = 2.5
FEATURE [Part::Cylinder] Cylinder690  label="Válec690"
  Angle = 360
  AttacherType = Attacher::AttachEngine3D
  Height = 20
  Placement = pos=(-23.55,-23.55,20) rot=(0,0,1;0rad)
  Radius = 2.5
FEATURE [Part::Cylinder] Cylinder699  label="Válec699"
  Angle = 360
  AttacherType = Attacher::AttachEngine3D
  Height = 20
  Placement = pos=(-23.55,23.55,20) rot=(0,0,1;0rad)
  Radius = 2.5
FEATURE [Part::Cylinder] Cylinder700  label="Válec700"
  Angle = 360
  AttacherType = Attacher::AttachEngine3D
  Height = 20
  Placement = pos=(23.55,23.55,20) rot=(0,0,1;0rad)
  Radius = 2.5
FEATURE [Part::Compound] Compound414
  Links = -> [Cylinder700,Cylinder699,Cylinder690,Cylinder694]
FEATURE [Part::Cylinder] Cylinder691  label="Válec691"
  Angle = 360
  AttacherType = Attacher::AttachEngine3D
  Height = 5
  Placement = pos=(16,0,2) rot=(0,0,1;3.53429rad)
  Radius = 3
FEATURE [Part::Cylinder] Cylinder688  label="Válec688"
  Angle = 360
  AttacherType = Attacher::AttachEngine3D
  Height = 5
  Placement = pos=(2e-15,16,2) rot=(0,0,-1;1.1781rad)
  Radius = 3
FEATURE [Part::Cylinder] Cylinder696  label="Válec696"
  Angle = 360
  AttacherType = Attacher::AttachEngine3D
  Height = 5
  Placement = pos=(-16,7e-15,2) rot=(0,0,1;0.392699rad)
  Radius = 3
FEATURE [Part::Cylinder] Cylinder692  label="Válec692"
  Angle = 360
  AttacherType = Attacher::AttachEngine3D
  Height = 5
  Placement = pos=(-1.2e-14,-16,2) rot=(0,0,1;1.96349rad)
  Radius = 3
FEATURE [Part::Compound] Compound416
  Links = -> [Cylinder692,Cylinder696,Cylinder688,Cylinder691]
  Placement = pos=(0,0,18) rot=(0,0,1;0.785398rad)
FEATURE [Part::Cylinder] Cylinder706  label="Válec706"
  Angle = 360
  AttacherType = Attacher::AttachEngine3D
  Height = 30
  Placement = pos=(16,0,2) rot=(0,0,1;3.53429rad)
  Radius = 1.5
FEATURE [Part::Cylinder] Cylinder695  label="Válec695"
  Angle = 360
  AttacherType = Attacher::AttachEngine3D
  Height = 30
  Placement = pos=(2e-15,16,2) rot=(0,0,-1;1.1781rad)
  Radius = 1.5
FEATURE [Part::Cylinder] Cylinder703  label="Válec703"
  Angle = 360
  AttacherType = Attacher::AttachEngine3D
  Height = 30
  Placement = pos=(-16,7e-15,2) rot=(0,0,1;0.392699rad)
  Radius = 1.5
FEATURE [Part::Cylinder] Cylinder701  label="Válec701"
  Angle = 360
  AttacherType = Attacher::AttachEngine3D
  Height = 30
  Placement = pos=(-1.2e-14,-16,2) rot=(0,0,1;1.96349rad)
  Radius = 1.5
FEATURE [Part::Compound] Compound412
  Links = -> [Cylinder701,Cylinder703,Cylinder695,Cylinder706]
  Placement = pos=(0,0,50) rot=(0,0,1;0.785398rad)
FEATURE [Part::Box] Box270  label="Krychle270"
  AttacherType = Attacher::AttachEngine3D
  Height = 8
  Length = 68
  Placement = pos=(-34,-32,26) rot=(0,0,1;0rad)
  Width = 64
FEATURE [Part::Cut] Cut275
  Base = -> Box270
  Tool = -> Compound412
FEATURE [Part::Cut] Cut274
  Base = -> Cut275
  Tool = -> Compound416
FEATURE [Part::Cut] Cut273
  Base = -> Cut274
  Tool = -> Compound414
FEATURE [Part::Cut] Cut278
  Base = -> Cut273
  Tool = -> Compound415
FEATURE [Part::Cut] Cut277
  Base = -> Cut278
  Tool = -> Cylinder697
FEATURE [Part::Cut] Cut276
  Base = -> Cut277
  Placement = pos=(0,0,-100) rot=(0,0,1;0rad)
  Tool = -> Compound413
FEATURE [Part::Cut] Cut279
  Base = -> Cut276
  Tool = -> Compound417
FEATURE [Part::Common] Common002
  Base = -> Cut279
  Tool = -> Box274
FEATURE [Part::Compound] Compound  label="bazovina-part-K_hold-in"
  Links = -> [Common003,Common002]
FEATURE [Part::Cylinder] Cylinder736  label="Válec736"
  Angle = 360
  AttacherType = Attacher::AttachEngine3D
  Height = 4
  Placement = pos=(23.55,23.55,26) rot=(0,0,1;0rad)
  Radius = 5
FEATURE [Part::Box] Box301  label="Krychle301"
  AttacherType = Attacher::AttachEngine3D
  Height = 3
  Length = 20
  Placement = pos=(17.55,-27.55,31) rot=(0,0,1;0rad)
  Width = 8
FEATURE [Part::Cylinder] Cylinder737  label="Válec737"
  Angle = 360
  AttacherType = Attacher::AttachEngine3D
  Height = 4
  Placement = pos=(23.55,-23.55,26) rot=(0,0,1;0rad)
  Radius = 5
FEATURE [Part::Cylinder] Cylinder738  label="Válec738"
  Angle = 360
  AttacherType = Attacher::AttachEngine3D
  Height = 20
  Placement = pos=(23.55,23.55,20) rot=(0,0,1;0rad)
  Radius = 2.5
FEATURE [Part::Cylinder] Cylinder739  label="Válec739"
  Angle = 360
  AttacherType = Attacher::AttachEngine3D
  Height = 5
  Placement = pos=(2e-15,16,2) rot=(0,0,-1;1.1781rad)
  Radius = 3
FEATURE [Part::Cylinder] Cylinder740  label="Válec740"
  Angle = 360
  AttacherType = Attacher::AttachEngine3D
  Height = 30
  Placement = pos=(16,0,2) rot=(0,0,1;3.53429rad)
  Radius = 1.5
FEATURE [Part::Box] Box302  label="Krychle302"
  AttacherType = Attacher::AttachEngine3D
  Height = 3
  Length = 20
  Placement = pos=(-37.45,19.55,31) rot=(0,0,1;0rad)
  Width = 8
FEATURE [Part::Cylinder] Cylinder741  label="Válec741"
  Angle = 360
  AttacherType = Attacher::AttachEngine3D
  Height = 5
  Placement = pos=(-1.2e-14,-16,2) rot=(0,0,1;1.96349rad)
  Radius = 3
FEATURE [Part::Cylinder] Cylinder742  label="Válec742"
  Angle = 360
  AttacherType = Attacher::AttachEngine3D
  Height = 5
  Placement = pos=(16,0,2) rot=(0,0,1;3.53429rad)
  Radius = 3
FEATURE [Part::Cylinder] Cylinder743  label="Válec743"
  Angle = 360
  AttacherType = Attacher::AttachEngine3D
  Height = 20
  Placement = pos=(0,0,15) rot=(0,0,1;0rad)
  Radius = 12
FEATURE [Part::Box] Box303  label="Krychle303"
  AttacherType = Attacher::AttachEngine3D
  Height = 2
  Length = 56
  Placement = pos=(-28,-28,-68) rot=(0,0,1;0rad)
  Width = 56
FEATURE [Part::Cylinder] Cylinder744  label="Válec744"
  Angle = 360
  AttacherType = Attacher::AttachEngine3D
  Height = 20
  Placement = pos=(15.75,114,59.48) rot=(0,0.707107,0.707107;3.14159rad)
  Radius = 1.5
FEATURE [Part::Cylinder] Cylinder745  label="Válec745"
  Angle = 360
  AttacherType = Attacher::AttachEngine3D
  Height = 20
  Placement = pos=(23.55,-23.55,20) rot=(0,0,1;0rad)
  Radius = 2.5
FEATURE [Part::Cylinder] Cylinder746  label="Válec746"
  Angle = 360
  AttacherType = Attacher::AttachEngine3D
  Height = 20
  Placement = pos=(-23.55,23.55,20) rot=(0,0,1;0rad)
  Radius = 2.5
FEATURE [Part::Cylinder] Cylinder747  label="Válec747"
  Angle = 360
  AttacherType = Attacher::AttachEngine3D
  Height = 4
  Placement = pos=(-23.55,23.55,26) rot=(0,0,1;0rad)
  Radius = 5
FEATURE [Part::Cylinder] Cylinder748  label="Válec748"
  Angle = 360
  AttacherType = Attacher::AttachEngine3D
  Height = 20
  Placement = pos=(15.75,114,38.52) rot=(0,0.707107,0.707107;3.14159rad)
  Radius = 1.5
FEATURE [Part::Compound] Compound443
  Links = -> [Cylinder748,Cylinder744]
  Placement = pos=(0,49,-200) rot=(1,0,0;1.5708rad)
FEATURE [Part::Box] Box304  label="Krychle304"
  AttacherType = Attacher::AttachEngine3D
  Height = 3
  Length = 20
  Placement = pos=(17.55,19.55,31) rot=(0,0,1;0rad)
  Width = 8
FEATURE [Part::Cylinder] Cylinder749  label="Válec749"
  Angle = 360
  AttacherType = Attacher::AttachEngine3D
  Height = 4
  Placement = pos=(-23.55,-23.55,26) rot=(0,0,1;0rad)
  Radius = 5
FEATURE [Part::Compound] Compound440
  Links = -> [Cylinder749,Cylinder736,Cylinder737,Cylinder747]
  Placement = pos=(0,0,-50) rot=(0,0,1;0rad)
FEATURE [Part::Cylinder] Cylinder750  label="Válec750"
  Angle = 360
  AttacherType = Attacher::AttachEngine3D
  Height = 20
  Placement = pos=(-23.55,-23.55,20) rot=(0,0,1;0rad)
  Radius = 2.5
FEATURE [Part::Compound] Compound445
  Links = -> [Cylinder738,Cylinder746,Cylinder750,Cylinder745]
FEATURE [Part::Box] Box305  label="Krychle305"
  AttacherType = Attacher::AttachEngine3D
  Height = 3
  Length = 20
  Placement = pos=(-37.45,-27.55,31) rot=(0,0,1;0rad)
  Width = 8
FEATURE [Part::Compound] Compound444
  Links = -> [Box304,Box301,Box302,Box305]
  Placement = pos=(0,0,-4) rot=(0,0,1;0rad)
FEATURE [Part::Cylinder] Cylinder751  label="Válec751"
  Angle = 360
  AttacherType = Attacher::AttachEngine3D
  Height = 5
  Placement = pos=(-16,7e-15,2) rot=(0,0,1;0.392699rad)
  Radius = 3
FEATURE [Part::Compound] Compound442
  Links = -> [Cylinder741,Cylinder751,Cylinder739,Cylinder742]
  Placement = pos=(0,0,18) rot=(0,0,1;0.785398rad)
FEATURE [Part::Cylinder] Cylinder752  label="Válec752"
  Angle = 360
  AttacherType = Attacher::AttachEngine3D
  Height = 30
  Placement = pos=(2e-15,16,2) rot=(0,0,-1;1.1781rad)
  Radius = 1.5
FEATURE [Part::Cylinder] Cylinder753  label="Válec753"
  Angle = 360
  AttacherType = Attacher::AttachEngine3D
  Height = 30
  Placement = pos=(-16,7e-15,2) rot=(0,0,1;0.392699rad)
  Radius = 1.5
FEATURE [Part::Cylinder] Cylinder754  label="Válec754"
  Angle = 360
  AttacherType = Attacher::AttachEngine3D
  Height = 30
  Placement = pos=(-1.2e-14,-16,2) rot=(0,0,1;1.96349rad)
  Radius = 1.5
FEATURE [Part::Compound] Compound441
  Links = -> [Cylinder754,Cylinder753,Cylinder752,Cylinder740]
  Placement = pos=(0,0,50) rot=(0,0,1;0.785398rad)
FEATURE [Part::Box] Box306  label="Krychle306"
  AttacherType = Attacher::AttachEngine3D
  Height = 8
  Length = 68
  Placement = pos=(-34,-32,26) rot=(0,0,1;0rad)
  Width = 64
FEATURE [Part::Cut] Cut299
  Base = -> Box306
  Tool = -> Compound441
FEATURE [Part::Cut] Cut295
  Base = -> Cut299
  Tool = -> Compound442
FEATURE [Part::Cut] Cut297
  Base = -> Cut295
  Tool = -> Compound445
FEATURE [Part::Cut] Cut301
  Base = -> Cut297
  Tool = -> Compound440
FEATURE [Part::Cut] Cut300
  Base = -> Cut301
  Tool = -> Cylinder743
FEATURE [Part::Cut] Cut296
  Base = -> Cut300
  Placement = pos=(0,0,-100) rot=(0,0,1;0rad)
  Tool = -> Compound444
FEATURE [Part::Cut] Cut298
  Base = -> Cut296
  Tool = -> Compound443
FEATURE [Part::Common] Common004
  Base = -> Cut298
  Tool = -> Box303
FEATURE [Part::Box] Box307  label="Krychle307"
  AttacherType = Attacher::AttachEngine3D
  Height = 40
  Length = 56
  Placement = pos=(28,-28,38) rot=(0,0,1;1.5708rad)
  Width = 56
FEATURE [Part::Cylinder] Cylinder755  label="Válec755"
  Angle = 360
  AttacherType = Attacher::AttachEngine3D
  Height = 50
  Placement = pos=(-23.55,23.55,20) rot=(0,0,1;0rad)
  Radius = 2.5
FEATURE [Part::Box] Box308  label="Krychle308"
  AttacherType = Attacher::AttachEngine3D
  Height = 9
  Length = 14.62
  Placement = pos=(-14.615,38,63) rot=(0,0,1;0rad)
  Width = 10
FEATURE [Part::Cylinder] Cylinder756  label="Válec756"
  Angle = 360
  AttacherType = Attacher::AttachEngine3D
  Height = 50
  Placement = pos=(23.55,23.55,20) rot=(0,0,1;0rad)
  Radius = 2.5
FEATURE [Part::Cylinder] Cylinder757  label="Válec757"
  Angle = 360
  AttacherType = Attacher::AttachEngine3D
  Height = 50
  Placement = pos=(23.55,-23.55,20) rot=(0,0,1;0rad)
  Radius = 2.5
FEATURE [Part::Box] Box309  label="Krychle309"
  AttacherType = Attacher::AttachEngine3D
  Height = 9
  Length = 38
  Placement = pos=(-48,-10,63) rot=(0,0,1;0rad)
  Width = 10
FEATURE [Part::Box] Box310  label="Krychle310"
  AttacherType = Attacher::AttachEngine3D
  Height = 9
  Length = 10
  Placement = pos=(-58,-10,63) rot=(0,0,1;0rad)
  Width = 48
FEATURE [Part::Box] Box311  label="Krychle311"
  AttacherType = Attacher::AttachEngine3D
  Height = 9
  Length = 10
  Placement = pos=(-10,-10,63) rot=(0,0,1;0rad)
  Width = 48
FEATURE [Part::Cylinder] Cylinder758  label="Válec758"
  Angle = 360
  AttacherType = Attacher::AttachEngine3D
  Height = 50
  Placement = pos=(-23.55,-23.55,20) rot=(0,0,1;0rad)
  Radius = 2.5
FEATURE [Part::Compound] Compound438
  Links = -> [Cylinder756,Cylinder757,Cylinder758,Cylinder755]
FEATURE [Part::Box] Box312  label="Krychle312"
  AttacherType = Attacher::AttachEngine3D
  Height = 9
  Length = 14.62
  Placement = pos=(-58,38,63) rot=(0,0,1;0rad)
  Width = 9
FEATURE [Part::Compound] Compound439
  Links = -> [Box312,Box311,Box310,Box308,Box309]
  Placement = pos=(29,-19,-4) rot=(0,0,1;0rad)
FEATURE [Part::Cut] Cut302
  Base = -> Compound439
  Tool = -> Compound438
FEATURE [Part::Common] Common005
  Base = -> Cut302
  Placement = pos=(0,0,-125) rot=(0,0,-1;1.5708rad)
  Tool = -> Box307
FEATURE [Part::Compound] Compound437  label="bazovina-part-K_hold-in001"
  Links = -> [Common004,Common005]
FEATURE [Part::Box] Box  label="Krychle"
  AttacherType = Attacher::AttachEngine3D
  Height = 2
  Length = 34
  Placement = pos=(-17,146,80) rot=(0,0,1;0rad)
  Width = 71
FEATURE [Part::Chamfer] Chamfer003
  Base = -> Box
  Edges = 2 edges r=8: [Edge3,Edge7]
FEATURE [Part::Box] Box313  label="Krychle313"
  AttacherType = Attacher::AttachEngine3D
  Height = 2
  Length = 68
  Placement = pos=(-34,120,80) rot=(0,0,1;0rad)
  Width = 26
FEATURE [Part::Chamfer] Chamfer004
  Base = -> Box313
  Edges = 1 edges r=2: [Edge3]
FEATURE [Part::Chamfer] Chamfer005
  Base = -> Chamfer004
  Edges = 1 edges r=2: [Edge15]
FEATURE [Part::Compound] Compound446  label="bazovina-part-K_hold-out-silo"
  Links = -> [Chamfer002,Chamfer003,Chamfer005]
FEATURE [Mesh::Feature] Mesh001  label="bazovina-part-K_hold-out-silo (Meshed)"
FEATURE [Mesh::Feature] Mesh  label="bazovina-part-K_hold-in001 (Meshed)"
FEATURE [Part::Box] Box314  label="Krychle314"
  AttacherType = Attacher::AttachEngine3D
  Height = 40
  Length = 56.5
  Placement = pos=(-28.25,-28.25,32) rot=(0,0,1;0rad)
  Width = 56.5
FEATURE [Part::Cylinder] Cylinder759  label="Válec759"
  Angle = 360
  AttacherType = Attacher::AttachEngine3D
  Height = 20
  Placement = pos=(23.55,-23.55,-34) rot=(0,0,1;0rad)
  Radius = 2.5
FEATURE [Part::Box] Box315  label="Krychle315"
  AttacherType = Attacher::AttachEngine3D
  Height = 20
  Length = 28.8
  Placement = pos=(-14.4,-8,34) rot=(0,0,1;0rad)
  Width = 43.38
FEATURE [Part::Cylinder] Cylinder760  label="Válec760"
  Angle = 360
  AttacherType = Attacher::AttachEngine3D
  Height = 20
  Placement = pos=(-23.55,23.55,-34) rot=(0,0,1;0rad)
  Radius = 2.5
FEATURE [Part::Box] Box316  label="Krychle316"
  AttacherType = Attacher::AttachEngine3D
  Height = 9
  Length = 64
  Placement = pos=(-32,-34,32) rot=(0,0,1;0rad)
  Width = 68
FEATURE [Part::Cut] Cut304
  Base = -> Box316
  Tool = -> Box314
FEATURE [Part::Box] Box317  label="Krychle317"
  AttacherType = Attacher::AttachEngine3D
  Height = 3
  Length = 20
  Placement = pos=(17.55,-27.55,-28) rot=(0,0,1;0rad)
  Width = 8
FEATURE [Part::Box] Box318  label="Krychle318"
  AttacherType = Attacher::AttachEngine3D
  Height = 3
  Length = 20
  Placement = pos=(17.55,19.55,-28) rot=(0,0,1;0rad)
  Width = 8
FEATURE [Part::Box] Box319  label="Krychle319"
  AttacherType = Attacher::AttachEngine3D
  Height = 3
  Length = 20
  Placement = pos=(-37.45,19.55,-28) rot=(0,0,1;0rad)
  Width = 8
FEATURE [Part::Box] Box320  label="Krychle320"
  AttacherType = Attacher::AttachEngine3D
  Height = 8
  Length = 68
  Placement = pos=(-34,-32,-30) rot=(0,0,1;0rad)
  Width = 64
FEATURE [Part::Cylinder] Cylinder772  label="Válec772"
  Angle = 360
  AttacherType = Attacher::AttachEngine3D
  Height = 3
  Placement = pos=(-24.02,-9.95,-30) rot=(0,0,1;1.96349rad)
  Radius = 3
FEATURE [Part::Cylinder] Cylinder767  label="Válec767"
  Angle = 360
  AttacherType = Attacher::AttachEngine3D
  Height = 20
  Placement = pos=(9.94977,-24.0209,-32) rot=(0,0,1;3.53429rad)
  Radius = 1.5
FEATURE [Part::Cylinder] Cylinder773  label="Válec773"
  Angle = 360
  AttacherType = Attacher::AttachEngine3D
  Height = 20
  Placement = pos=(23.55,23.55,-34) rot=(0,0,1;0rad)
  Radius = 2.5
FEATURE [Part::Cylinder] Cylinder768  label="Válec768"
  Angle = 360
  AttacherType = Attacher::AttachEngine3D
  Height = 20
  Placement = pos=(24.0209,-9.94977,-32) rot=(0,0,-1;1.96349rad)
  Radius = 1.5
FEATURE [Part::Cylinder] Cylinder774  label="Válec774"
  Angle = 360
  AttacherType = Attacher::AttachEngine3D
  Height = 20
  Placement = pos=(-23.55,-23.55,-34) rot=(0,0,1;0rad)
  Radius = 2.5
FEATURE [Part::Cylinder] Cylinder775  label="Válec775"
  Angle = 360
  AttacherType = Attacher::AttachEngine3D
  Height = 3
  Placement = pos=(-9.95,24.02,-30) rot=(0,0,1;0.392699rad)
  Radius = 3
FEATURE [Part::Cylinder] Cylinder776  label="Válec776"
  Angle = 360
  AttacherType = Attacher::AttachEngine3D
  Height = 3
  Placement = pos=(9.95,-24.02,-30) rot=(0,0,1;3.53429rad)
  Radius = 3
FEATURE [Part::Cylinder] Cylinder777  label="Válec777"
  Angle = 360
  AttacherType = Attacher::AttachEngine3D
  Height = 3
  Placement = pos=(24.02,9.95,-30) rot=(0,0,-1;1.1781rad)
  Radius = 3
FEATURE [Part::Box] Box321  label="Krychle321"
  AttacherType = Attacher::AttachEngine3D
  Height = 3
  Length = 20
  Placement = pos=(-37.45,-27.55,-28) rot=(0,0,1;0rad)
  Width = 8
FEATURE [Part::Cylinder] Cylinder765  label="Válec765"
  Angle = 360
  AttacherType = Attacher::AttachEngine3D
  Height = 20
  Placement = pos=(-24.0209,-9.94977,-32) rot=(0,0,1;1.96349rad)
  Radius = 1.5
FEATURE [Part::Cylinder] Cylinder778  label="Válec778"
  Angle = 360
  AttacherType = Attacher::AttachEngine3D
  Height = 20
  Placement = pos=(0,0,-39) rot=(0,0,1;0rad)
  Radius = 12
FEATURE [Part::Cylinder] Cylinder764  label="Válec764"
  Angle = 360
  AttacherType = Attacher::AttachEngine3D
  Height = 20
  Placement = pos=(-24.0209,9.94977,-32) rot=(0,0,1;1.1781rad)
  Radius = 1.5
FEATURE [Part::Cylinder] Cylinder781  label="Válec781"
  Angle = 360
  AttacherType = Attacher::AttachEngine3D
  Height = 20
  Placement = pos=(-15.75,10.48,-35) rot=(0,0,1;0rad)
  Radius = 2
FEATURE [Part::Cylinder] Cylinder782  label="Válec782"
  Angle = 360
  AttacherType = Attacher::AttachEngine3D
  Height = 20
  Placement = pos=(-9.94977,24.0209,-32) rot=(0,0,1;0.392699rad)
  Radius = 1.5
FEATURE [Part::Cylinder] Cylinder771  label="Válec771"
  Angle = 360
  AttacherType = Attacher::AttachEngine3D
  Height = 3
  Placement = pos=(-24.0204,9.94899,-30) rot=(0,0,1;1.1781rad)
  Radius = 3
FEATURE [Part::Cylinder] Cylinder769  label="Válec769"
  Angle = 360
  AttacherType = Attacher::AttachEngine3D
  Height = 20
  Placement = pos=(24.0209,9.94977,-32) rot=(0,0,-1;1.1781rad)
  Radius = 1.5
FEATURE [Part::Cylinder] Cylinder766  label="Válec766"
  Angle = 360
  AttacherType = Attacher::AttachEngine3D
  Height = 20
  Placement = pos=(-9.94977,-24.0209,-32) rot=(0,0,1;2.74889rad)
  Radius = 1.5
FEATURE [Part::Cylinder] Cylinder780  label="Válec780"
  Angle = 360
  AttacherType = Attacher::AttachEngine3D
  Height = 20
  Placement = pos=(-15.75,-10.48,-35) rot=(0,0,1;0rad)
  Radius = 2
FEATURE [Part::Cylinder] Cylinder783  label="Válec783"
  Angle = 360
  AttacherType = Attacher::AttachEngine3D
  Height = 3
  Placement = pos=(9.94899,24.0204,-30) rot=(0,0,-1;0.392699rad)
  Radius = 3
FEATURE [Part::Cylinder] Cylinder784  label="Válec784"
  Angle = 360
  AttacherType = Attacher::AttachEngine3D
  Height = 3
  Placement = pos=(-9.94899,-24.0204,-30) rot=(0,0,1;2.74889rad)
  Radius = 3
FEATURE [Part::Box] Box322  label="Krychle322"
  AttacherType = Attacher::AttachEngine3D
  Height = 61
  Length = 32
  Placement = pos=(-16,28.25,-83) rot=(0,0,1;0rad)
  Width = 6
FEATURE [Part::Cylinder] Cylinder785  label="Válec785"
  Angle = 360
  AttacherType = Attacher::AttachEngine3D
  Height = 3
  Placement = pos=(24.0204,-9.94899,-30) rot=(0,0,-1;1.96349rad)
  Radius = 3
FEATURE [Part::Cylinder] Cylinder770  label="Válec770"
  Angle = 360
  AttacherType = Attacher::AttachEngine3D
  Height = 20
  Placement = pos=(9.94977,24.0209,-32) rot=(0,0,-1;0.392699rad)
  Radius = 1.5
FEATURE [Part::Compound] Compound533
  Links = -> [Cylinder775,Cylinder771,Cylinder772,Cylinder784,Cylinder776,Cylinder785,Cylinder777,Cylinder783]
FEATURE [Part::Compound] Compound534
  Links = -> [Cylinder780,Cylinder781]
FEATURE [Part::Compound] Compound532
  Links = -> [Cylinder782,Cylinder764,Cylinder765,Cylinder766,Cylinder767,Cylinder768,Cylinder769,Cylinder770]
FEATURE [Part::Compound] Compound529  label="hrubo_holder020"
  Links = -> [Cut304]
FEATURE [Part::Compound] Compound526
  Links = -> [Box318,Box317,Box319,Box321]
FEATURE [Part::Cut] Cut309
  Base = -> Box320
  Tool = -> Compound526
FEATURE [Part::Compound] Compound528  label="hrubo_holder019"
  Links = -> [Compound529]
FEATURE [Part::Cut] Cut305
  Base = -> Compound528
  Placement = pos=(-29,18,30) rot=(0,0,1;0rad)
  Tool = -> Box315
FEATURE [Part::Compound] Compound530
  Links = -> [Cut305]
  Placement = pos=(18,-29,32) rot=(0.707107,-0.707107,0;3.14159rad)
FEATURE [Part::Compound] Compound527
  Links = -> [Cylinder773,Cylinder760,Cylinder774,Cylinder759]
FEATURE [Part::Cut] Cut310
  Base = -> Cut309
  Tool = -> Compound527
FEATURE [Part::Cut] Cut303
  Base = -> Cut310
  Tool = -> Cylinder778
FEATURE [Part::Cut] Cut307
  Base = -> Cut303
  Tool = -> Compound532
FEATURE [Part::Cut] Cut308
  Base = -> Cut307
  Tool = -> Compound533
FEATURE [Part::Cut] Cut311
  Base = -> Cut308
  Tool = -> Compound534
FEATURE [Part::Compound] Compound535
  Links = -> [Cut311,Box322]
FEATURE [Part::Compound] Compound536  label="gearovina_midi_motohold_hrubo"
  Links = -> [Compound530,Compound535]
FEATURE [Part::Chamfer] Chamfer007
  Base = -> Compound536
  Edges = 4 edges r=4: [Edge3,Edge18,Edge37,Edge40]
FEATURE [Part::Chamfer] Chamfer011
  Base = -> Chamfer007
  Edges = 4 edges r=4: [Edge2,Edge21,Edge117,Edge118]
FEATURE [Part::Chamfer] Chamfer006
  Base = -> Chamfer011
  Edges = 2 edges r=2: [Edge6,Edge10]
FEATURE [Part::Chamfer] Chamfer008
  Base = -> Chamfer006
  Edges = 2 edges r=1: [Edge4,Edge16]
FEATURE [Part::Chamfer] Chamfer009
  Base = -> Chamfer008
  Edges = 2 edges r=8: [Edge217,Edge221]
FEATURE [Part::Chamfer] Chamfer012  label="gearovina_midi_motohold2"
  Base = -> Chamfer009
  Edges = 2 edges r=2: [Edge3,Edge15]
FEATURE [Part::Chamfer] Chamfer010  label="Base_moto-hold-old"
  Base = -> Chamfer012
  Edges = 1 edges r=2: [Edge38]
  Placement = pos=(0,0,-15) rot=(0,0,1;0rad)
FEATURE [Part::Cylinder] Cylinder1860  label="Válec1860"
  Angle = 360
  AttacherType = Attacher::AttachEngine3D
  Height = 20
  Placement = pos=(-23.55,-23.55,-34) rot=(0,0,1;0rad)
  Radius = 2.5
FEATURE [Part::Cylinder] Cylinder1862  label="Válec1862"
  Angle = 360
  AttacherType = Attacher::AttachEngine3D
  Height = 20
  Placement = pos=(-23.55,23.55,-34) rot=(0,0,1;0rad)
  Radius = 2.5
FEATURE [Part::Cylinder] Cylinder1861  label="Válec1861"
  Angle = 360
  AttacherType = Attacher::AttachEngine3D
  Height = 20
  Placement = pos=(23.55,23.55,-34) rot=(0,0,1;0rad)
  Radius = 2.5
FEATURE [Part::Cylinder] Cylinder1856  label="Válec1856"
  Angle = 360
  AttacherType = Attacher::AttachEngine3D
  Height = 1.75
  Placement = pos=(-23.55,-23.55,-34) rot=(0,0,1;0rad)
  Radius = 7
FEATURE [Part::Cylinder] Cylinder1857  label="Válec1857"
  Angle = 360
  AttacherType = Attacher::AttachEngine3D
  Height = 1.75
  Placement = pos=(23.55,23.55,-34) rot=(0,0,1;0rad)
  Radius = 7
FEATURE [Part::Cylinder] Cylinder1858  label="Válec1858"
  Angle = 360
  AttacherType = Attacher::AttachEngine3D
  Height = 1.75
  Placement = pos=(-23.55,23.55,-34) rot=(0,0,1;0rad)
  Radius = 7
FEATURE [Part::Cylinder] Cylinder1859  label="Válec1859"
  Angle = 360
  AttacherType = Attacher::AttachEngine3D
  Height = 20
  Placement = pos=(23.55,-23.55,-34) rot=(0,0,1;0rad)
  Radius = 2.5
FEATURE [Part::Compound] Compound930
  Links = -> [Cylinder1861,Cylinder1862,Cylinder1860,Cylinder1859]
  Placement = pos=(0,0,-8) rot=(0,0,1;0rad)
FEATURE [Part::Box] Box323  label="Krychle323"
  AttacherType = Attacher::AttachEngine3D
  Height = 3
  Length = 20
  Placement = pos=(17.55,19.55,-28) rot=(0,0,1;0rad)
  Width = 8
FEATURE [Part::Cylinder] Cylinder1863  label="Válec1863"
  Angle = 360
  AttacherType = Attacher::AttachEngine3D
  Height = 20
  Placement = pos=(23.55,-23.55,-34) rot=(0,0,1;0rad)
  Radius = 2.5
FEATURE [Part::Box] Box324  label="Krychle324"
  AttacherType = Attacher::AttachEngine3D
  Height = 3
  Length = 20
  Placement = pos=(17.55,-27.55,-28) rot=(0,0,1;0rad)
  Width = 8
FEATURE [Part::Box] Box325  label="Krychle325"
  AttacherType = Attacher::AttachEngine3D
  Height = 40
  Length = 56.5
  Placement = pos=(-28.25,-28.25,32) rot=(0,0,1;0rad)
  Width = 56.5
FEATURE [Part::Cylinder] Cylinder1864  label="Válec1864"
  Angle = 360
  AttacherType = Attacher::AttachEngine3D
  Height = 20
  Placement = pos=(-23.55,-23.55,-34) rot=(0,0,1;0rad)
  Radius = 2.5
FEATURE [Part::Box] Box326  label="Krychle326"
  AttacherType = Attacher::AttachEngine3D
  Height = 61
  Length = 32
  Placement = pos=(-16,28.25,-83) rot=(0,0,1;0rad)
  Width = 4.75
FEATURE [Part::Box] Box327  label="Krychle327"
  AttacherType = Attacher::AttachEngine3D
  Height = 9
  Length = 65
  Placement = pos=(-33,-34,32) rot=(0,0,1;0rad)
  Width = 68
FEATURE [Part::Cut] Cut313
  Base = -> Box327
  Tool = -> Box325
FEATURE [Part::Compound] Compound927  label="hrubo_holder022"
  Links = -> [Cut313]
FEATURE [Part::Compound] Compound926  label="hrubo_holder021"
  Links = -> [Compound927]
FEATURE [Part::Cylinder] Cylinder1847  label="Válec1847"
  Angle = 360
  AttacherType = Attacher::AttachEngine3D
  Height = 40
  Placement = pos=(0,140,65) rot=(1,0,0;1.5708rad)
  Radius = 1.5
FEATURE [Part::Cylinder] Cylinder1865  label="Válec1865"
  Angle = 360
  AttacherType = Attacher::AttachEngine3D
  Height = 20
  Placement = pos=(23.55,23.55,-34) rot=(0,0,1;0rad)
  Radius = 2.5
FEATURE [Part::Box] Box328  label="Krychle328"
  AttacherType = Attacher::AttachEngine3D
  Height = 3
  Length = 20
  Placement = pos=(-37.45,19.55,-28) rot=(0,0,1;0rad)
  Width = 8
FEATURE [Part::Cylinder] Cylinder1866  label="Válec1866"
  Angle = 360
  AttacherType = Attacher::AttachEngine3D
  Height = 20
  Placement = pos=(-23.55,23.55,-34) rot=(0,0,1;0rad)
  Radius = 2.5
FEATURE [Part::Box] Box329  label="Krychle329"
  AttacherType = Attacher::AttachEngine3D
  Height = 8
  Length = 68
  Placement = pos=(-34,-32,-30) rot=(0,0,1;0rad)
  Width = 65
FEATURE [Part::Box] Box330  label="Krychle330"
  AttacherType = Attacher::AttachEngine3D
  Height = 3
  Length = 20
  Placement = pos=(-37.45,-27.55,-28) rot=(0,0,1;0rad)
  Width = 8
FEATURE [Part::Cylinder] Cylinder1867  label="Válec1867"
  Angle = 360
  AttacherType = Attacher::AttachEngine3D
  Height = 20
  Placement = pos=(0,0,-39) rot=(0,0,1;0rad)
  Radius = 12
FEATURE [Part::Box] Box331  label="Krychle331"
  AttacherType = Attacher::AttachEngine3D
  Height = 20
  Length = 28.8
  Placement = pos=(-14.4,-8,34) rot=(0,0,1;0rad)
  Width = 43.38
FEATURE [Part::Cut] Cut316
  Base = -> Compound926
  Placement = pos=(-29,18,30) rot=(0,0,1;0rad)
  Tool = -> Box331
FEATURE [Part::Compound] Compound928
  Links = -> [Cut316]
  Placement = pos=(18,-29,32) rot=(0.707107,-0.707107,0;3.14159rad)
FEATURE [Part::Chamfer] Chamfer013
  Base = -> Compound928
  Edges = 5 edges r=2: [Edge2,Edge7,Edge8,Edge16,Edge17]
FEATURE [Part::Cylinder] Cylinder1848  label="Válec1848"
  Angle = 360
  AttacherType = Attacher::AttachEngine3D
  Height = 40
  Placement = pos=(16,140,49) rot=(1,0,0;1.5708rad)
  Radius = 1.5
FEATURE [Part::Cylinder] Cylinder1850  label="Válec1850"
  Angle = 360
  AttacherType = Attacher::AttachEngine3D
  Height = 40
  Placement = pos=(-16,140,49) rot=(1,0,0;1.5708rad)
  Radius = 1.5
FEATURE [Part::Cylinder] Cylinder1849  label="Válec1849"
  Angle = 360
  AttacherType = Attacher::AttachEngine3D
  Height = 40
  Placement = pos=(0,140,33) rot=(1,0,0;1.5708rad)
  Radius = 1.5
FEATURE [Part::Compound] Compound925
  Links = -> [Cylinder1847,Cylinder1848,Cylinder1850,Cylinder1849]
  Placement = pos=(-34.65,34.65,-144) rot=(0.862856,0.357407,0.357407;1.71777rad)
FEATURE [Part::Cylinder] Cylinder1851  label="Válec1851"
  Angle = 360
  AttacherType = Attacher::AttachEngine3D
  Height = 3
  Placement = pos=(0,140,65) rot=(1,0,0;1.5708rad)
  Radius = 3
FEATURE [Part::Cylinder] Cylinder1853  label="Válec1853"
  Angle = 360
  AttacherType = Attacher::AttachEngine3D
  Height = 3
  Placement = pos=(-16,140,49) rot=(1,0,0;1.5708rad)
  Radius = 3
FEATURE [Part::Cylinder] Cylinder1852  label="Válec1852"
  Angle = 360
  AttacherType = Attacher::AttachEngine3D
  Height = 3
  Placement = pos=(16,140,49) rot=(1,0,0;1.5708rad)
  Radius = 3
FEATURE [Part::Cylinder] Cylinder1854  label="Válec1854"
  Angle = 360
  AttacherType = Attacher::AttachEngine3D
  Height = 3
  Placement = pos=(0,140,33) rot=(1,0,0;1.5708rad)
  Radius = 3
FEATURE [Part::Cylinder] Cylinder1855  label="Válec1855"
  Angle = 360
  AttacherType = Attacher::AttachEngine3D
  Height = 1.75
  Placement = pos=(23.55,-23.55,-34) rot=(0,0,1;0rad)
  Radius = 7
FEATURE [Part::Compound] Compound929
  Links = -> [Cylinder1857,Cylinder1858,Cylinder1856,Cylinder1855]
  Placement = pos=(0,0,-0.75) rot=(0,0,1;0rad)
FEATURE [Part::Compound] Compound931
  Links = -> [Cylinder1865,Cylinder1866,Cylinder1864,Cylinder1863]
FEATURE [Part::Compound] Compound932
  Links = -> [Box323,Box324,Box328,Box330]
FEATURE [Part::Cut] Cut314
  Base = -> Box329
  Tool = -> Compound932
FEATURE [Part::Cut] Cut317
  Base = -> Cut314
  Tool = -> Compound931
FEATURE [Part::Cut] Cut315
  Base = -> Cut317
  Tool = -> Cylinder1867
FEATURE [Part::Chamfer] Chamfer015
  Base = -> Box326
  Edges = 2 edges r=8: [Edge4,Edge8]
FEATURE [Part::Compound] Compound933
  Links = -> [Cylinder1851,Cylinder1852,Cylinder1853,Cylinder1854]
  Placement = pos=(-34.65,34.65,-167) rot=(0.862856,0.357407,0.357407;1.71777rad)
FEATURE [Part::Cut] Cut318
  Base = -> Compound929
  Placement = pos=(0,0,3) rot=(0,0,1;0rad)
  Tool = -> Compound930
FEATURE [Part::Cut] Cut319
  Base = -> Cut315
  Tool = -> Compound925
FEATURE [Part::Cut] Cut312
  Base = -> Cut319
  Tool = -> Compound933
FEATURE [Part::Chamfer] Chamfer014
  Base = -> Cut312
  Edges = 1 edges r=4: [Edge15]
FEATURE [Part::Compound] Compound934  label="Base_moto-hold"
  Links = -> [Cut318,Chamfer013,Chamfer015,Chamfer014]
FEATURE [Mesh::Feature] Mesh002  label="Base_moto-hold (Meshed)"
